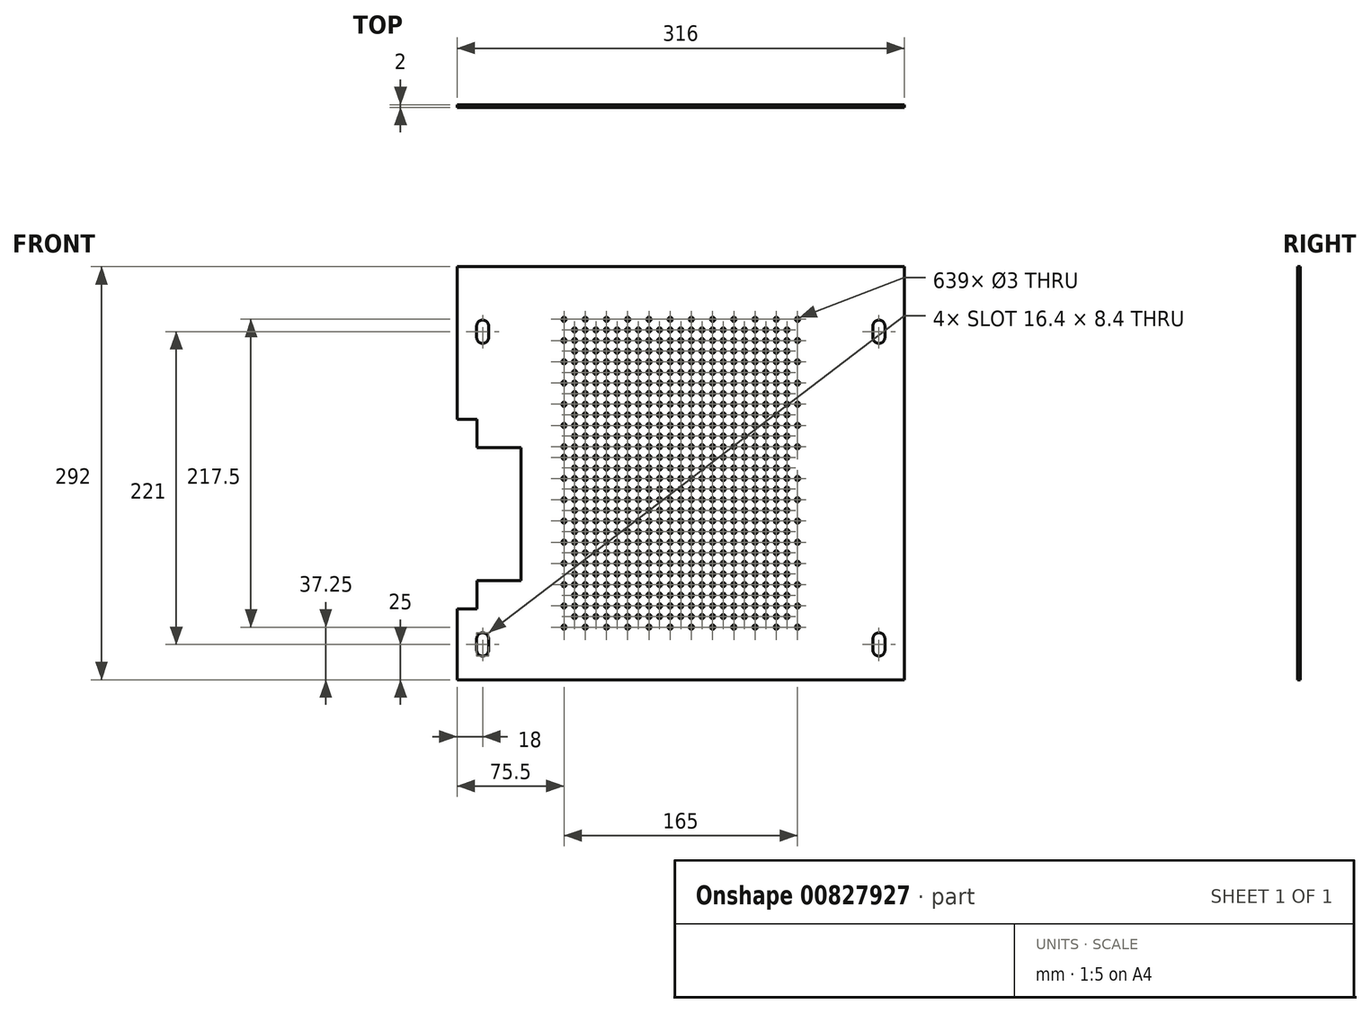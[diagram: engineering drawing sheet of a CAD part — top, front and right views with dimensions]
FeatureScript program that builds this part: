
annotation { "Feature Type Name" : "Feature", "Feature Type Description" : "" }
export const myFeature = defineFeature(function(context is Context, id is Id, definition is map)
    precondition{}
    {
        {
            var Q0;
            Q0=qCreatedBy(makeId("Front.planeOp"),FACE);
            var sketch = newSketch(context, id + "F0", { "sketchPlane" : qUnion([Q0])});
            skLineSegment(sketch, "E0.bottom", {"start": v(158, 146) * mm, "end": v(-158, 146) * mm});
            skLineSegment(sketch, "E0.top", {"start": v(158, -146) * mm, "end": v(-158, -146) * mm});
            skLineSegment(sketch, "E0.left", {"start": v(158, 146) * mm, "end": v(158, -146) * mm});
            skLineSegment(sketch, "E0.right", {"start": v(-158, 146) * mm, "end": v(-158, 38) * mm});
            skPoint(sketch, "E0.middle", {"position": v(0, 0) * mm});
            skLineSegment(sketch, "E1", {"start": v(-113, 18) * mm, "end": v(-113, -76) * mm});
            skLineSegment(sketch, "E2.trimOffspring", {"start": v(-158, -96) * mm, "end": v(-158, -146) * mm});
            skLineSegment(sketch, "E3", {"start": v(-158, 38) * mm, "end": v(-144, 38) * mm});
            skLineSegment(sketch, "E4", {"start": v(-144, 38) * mm, "end": v(-144, 18) * mm});
            skLineSegment(sketch, "E5", {"start": v(-144, 18) * mm, "end": v(-113, 18) * mm});
            skLineSegment(sketch, "E6", {"start": v(-113, -76) * mm, "end": v(-144, -76) * mm});
            skLineSegment(sketch, "E7", {"start": v(-144, -76) * mm, "end": v(-144, -96) * mm});
            skLineSegment(sketch, "E8", {"start": v(-144, -96) * mm, "end": v(-158, -96) * mm});
            skSolve(sketch);
        }
        {
            var Q0;
            Q0 = qSketchRegion(id + "F0", true);
            extrude(context, id + "F1", {"entities" : qUnion([Q0]), "depth" : 2 * mm, "offsetDistance" : 25 * mm});
        }
        {
            var Q0;
            Q0=makeQuery(id+"F1.opExtrude","CAP_FACE",FACE,{"disambiguationData":[OSD([sQuery(id+"F0.wireOp",EDGE,"E0.bottom"),sQuery(id+"F0.wireOp",EDGE,"E0.top"),sQuery(id+"F0.wireOp",EDGE,"E0.left"),sQuery(id+"F0.wireOp",EDGE,"E0.right"),sQuery(id+"F0.wireOp",EDGE,"E1"),sQuery(id+"F0.wireOp",EDGE,"E2.trimOffspring"),sQuery(id+"F0.wireOp",EDGE,"E3"),sQuery(id+"F0.wireOp",EDGE,"E4"),sQuery(id+"F0.wireOp",EDGE,"E5"),sQuery(id+"F0.wireOp",EDGE,"E6"),sQuery(id+"F0.wireOp",EDGE,"E7"),sQuery(id+"F0.wireOp",EDGE,"E8")])],"isStart":false});
            var sketch = newSketch(context, id + "F2", { "sketchPlane" : qUnion([Q0])});
            skLineSegment(sketch, "E9", {"start": v(-140, 100) * mm, "end": v(-140, 104) * mm});
            skLineSegment(sketch, "E10", {"start": v(-140, 100) * mm, "end": v(-140, 96) * mm});
            skArc(sketch, "E11.0.endCap", {"start": v(-144.2, 104) * mm, "mid": v(-140, 108.2) * mm, "end": v(-135.8, 104) * mm});
            skLineSegment(sketch, "E11.0.left", {"start": v(-144.2, 100) * mm, "end": v(-144.2, 104) * mm});
            skLineSegment(sketch, "E11.0.right", {"start": v(-135.8, 100) * mm, "end": v(-135.8, 104) * mm});
            skArc(sketch, "E11.1.endCap", {"start": v(-135.8, 96) * mm, "mid": v(-140, 91.8) * mm, "end": v(-144.2, 96) * mm});
            skLineSegment(sketch, "E11.1.left", {"start": v(-135.8, 100) * mm, "end": v(-135.8, 96) * mm});
            skLineSegment(sketch, "E11.1.right", {"start": v(-144.2, 100) * mm, "end": v(-144.2, 96) * mm});
            skLineSegment(sketch, "E12.MirrorCS", {"start": v(144.2, 100) * mm, "end": v(144.2, 104) * mm});
            skArc(sketch, "E13.MirrorCS", {"start": v(144.2, 104) * mm, "mid": v(140, 108.2) * mm, "end": v(135.8, 104) * mm});
            skLineSegment(sketch, "E14.MirrorCS", {"start": v(135.8, 100) * mm, "end": v(135.8, 104) * mm});
            skLineSegment(sketch, "E15.MirrorCS", {"start": v(135.8, 100) * mm, "end": v(135.8, 96) * mm});
            skArc(sketch, "E16.MirrorCS", {"start": v(135.8, 96) * mm, "mid": v(140, 91.8) * mm, "end": v(144.2, 96) * mm});
            skLineSegment(sketch, "E17.MirrorCS", {"start": v(144.2, 100) * mm, "end": v(144.2, 96) * mm});
            skLineSegment(sketch, "E18", {"start": v(-140, -125) * mm, "end": v(-140, -117) * mm});
            skArc(sketch, "E19.0.startCap", {"start": v(-135.8, -125) * mm, "mid": v(-140, -129.2) * mm, "end": v(-144.2, -125) * mm});
            skArc(sketch, "E19.0.endCap", {"start": v(-144.2, -117) * mm, "mid": v(-140, -112.8) * mm, "end": v(-135.8, -117) * mm});
            skLineSegment(sketch, "E19.0.left", {"start": v(-144.2, -125) * mm, "end": v(-144.2, -117) * mm});
            skLineSegment(sketch, "E19.0.right", {"start": v(-135.8, -125) * mm, "end": v(-135.8, -117) * mm});
            skArc(sketch, "E20.MirrorCS", {"start": v(135.8, -125) * mm, "mid": v(140, -129.2) * mm, "end": v(144.2, -125) * mm});
            skLineSegment(sketch, "E21.MirrorCS", {"start": v(135.8, -125) * mm, "end": v(135.8, -117) * mm});
            skLineSegment(sketch, "E22.MirrorCS", {"start": v(144.2, -125) * mm, "end": v(144.2, -117) * mm});
            skArc(sketch, "E23.MirrorCS", {"start": v(144.2, -117) * mm, "mid": v(140, -112.8) * mm, "end": v(135.8, -117) * mm});
            skSolve(sketch);
        }
        {
            var Q0;
            Q0 = qSketchRegion(id + "F2", true);
            extrude(context, id + "F3", {"entities" : qUnion([Q0]), "operationType" : NewBodyOperationType.REMOVE, "endBound" : BoundingType.THROUGH_ALL, "oppositeDirection" : true, "depth" : 25 * mm, "offsetDistance" : 25 * mm});
        }
        {
            var Q0;
            Q0=makeQuery(id+"F1.opExtrude","CAP_FACE",FACE,{"disambiguationData":[OSD([sQuery(id+"F0.wireOp",EDGE,"E0.bottom"),sQuery(id+"F0.wireOp",EDGE,"E0.top"),sQuery(id+"F0.wireOp",EDGE,"E0.left"),sQuery(id+"F0.wireOp",EDGE,"E0.right"),sQuery(id+"F0.wireOp",EDGE,"E1"),sQuery(id+"F0.wireOp",EDGE,"E2.trimOffspring"),sQuery(id+"F0.wireOp",EDGE,"E3"),sQuery(id+"F0.wireOp",EDGE,"E4"),sQuery(id+"F0.wireOp",EDGE,"E5"),sQuery(id+"F0.wireOp",EDGE,"E6"),sQuery(id+"F0.wireOp",EDGE,"E7"),sQuery(id+"F0.wireOp",EDGE,"E8")])],"isStart":false});
            var sketch = newSketch(context, id + "F4", { "sketchPlane" : qUnion([Q0])});
            skLineSegment(sketch, "E24", {"start": v(0, 0) * mm, "end": v(0, 20.25) * mm});
            skCircle(sketch, "E25", {"center": v(0, 3.75) * mm, "radius": 1.5 * mm});
            skCircle(sketch, "E26.0.1.0", {"center": v(0, 11.25) * mm, "radius": 1.5 * mm});
            skCircle(sketch, "E26.0.2.0", {"center": v(0, 18.75) * mm, "radius": 1.5 * mm});
            skCircle(sketch, "E26.0.3.0", {"center": v(0, 26.25) * mm, "radius": 1.5 * mm});
            skCircle(sketch, "E26.0.4.0", {"center": v(0, 33.75) * mm, "radius": 1.5 * mm});
            skCircle(sketch, "E26.0.5.0", {"center": v(0, 41.25) * mm, "radius": 1.5 * mm});
            skCircle(sketch, "E26.0.6.0", {"center": v(0, 48.75) * mm, "radius": 1.5 * mm});
            skCircle(sketch, "E26.0.7.0", {"center": v(0, 56.25) * mm, "radius": 1.5 * mm});
            skCircle(sketch, "E26.0.8.0", {"center": v(0, 63.75) * mm, "radius": 1.5 * mm});
            skCircle(sketch, "E26.0.9.0", {"center": v(0, 71.25) * mm, "radius": 1.5 * mm});
            skCircle(sketch, "E26.0.10.0", {"center": v(0, 78.75) * mm, "radius": 1.5 * mm});
            skCircle(sketch, "E26.0.11.0", {"center": v(0, 86.25) * mm, "radius": 1.5 * mm});
            skCircle(sketch, "E26.0.12.0", {"center": v(0, 93.75) * mm, "radius": 1.5 * mm});
            skCircle(sketch, "E26.0.13.0", {"center": v(0, 101.25) * mm, "radius": 1.5 * mm});
            skLineSegment(sketch, "E26.direction1", {"start": v(0, 3.75) * mm, "end": v(25, 3.75) * mm, "construction": true});
            skLineSegment(sketch, "E26.direction2", {"start": v(0, 3.75) * mm, "end": v(0, 11.25) * mm, "construction": true});
            skLineSegment(sketch, "E27.1.0.0", {"start": v(7.5, 3.75) * mm, "end": v(7.5, 11.25) * mm, "construction": true});
            skCircle(sketch, "E27.1.0.1", {"center": v(7.5, 86.25) * mm, "radius": 1.5 * mm});
            skCircle(sketch, "E27.1.0.2", {"center": v(7.5, 26.25) * mm, "radius": 1.5 * mm});
            skCircle(sketch, "E27.1.0.3", {"center": v(7.5, 48.75) * mm, "radius": 1.5 * mm});
            skCircle(sketch, "E27.1.0.4", {"center": v(7.5, 101.25) * mm, "radius": 1.5 * mm});
            skCircle(sketch, "E27.1.0.5", {"center": v(7.5, 108.75) * mm, "radius": 1.5 * mm});
            skCircle(sketch, "E27.1.0.6", {"center": v(7.5, 93.75) * mm, "radius": 1.5 * mm});
            skCircle(sketch, "E27.1.0.7", {"center": v(7.5, 18.75) * mm, "radius": 1.5 * mm});
            skCircle(sketch, "E27.1.0.8", {"center": v(7.5, 63.75) * mm, "radius": 1.5 * mm});
            skCircle(sketch, "E27.1.0.9", {"center": v(7.5, 71.25) * mm, "radius": 1.5 * mm});
            skCircle(sketch, "E27.1.0.10", {"center": v(7.5, 56.25) * mm, "radius": 1.5 * mm});
            skCircle(sketch, "E27.1.0.11", {"center": v(7.5, 41.25) * mm, "radius": 1.5 * mm});
            skCircle(sketch, "E27.1.0.12", {"center": v(7.5, 33.75) * mm, "radius": 1.5 * mm});
            skCircle(sketch, "E27.1.0.13", {"center": v(7.5, 78.75) * mm, "radius": 1.5 * mm});
            skCircle(sketch, "E27.1.0.14", {"center": v(7.5, 11.25) * mm, "radius": 1.5 * mm});
            skCircle(sketch, "E27.1.0.15", {"center": v(7.5, 3.75) * mm, "radius": 1.5 * mm});
            skLineSegment(sketch, "E27.2.0.0", {"start": v(15, 3.75) * mm, "end": v(15, 11.25) * mm, "construction": true});
            skCircle(sketch, "E27.2.0.1", {"center": v(15, 86.25) * mm, "radius": 1.5 * mm});
            skCircle(sketch, "E27.2.0.2", {"center": v(15, 26.25) * mm, "radius": 1.5 * mm});
            skCircle(sketch, "E27.2.0.3", {"center": v(15, 48.75) * mm, "radius": 1.5 * mm});
            skCircle(sketch, "E27.2.0.4", {"center": v(15, 101.25) * mm, "radius": 1.5 * mm});
            skCircle(sketch, "E27.2.0.6", {"center": v(15, 93.75) * mm, "radius": 1.5 * mm});
            skCircle(sketch, "E27.2.0.7", {"center": v(15, 18.75) * mm, "radius": 1.5 * mm});
            skCircle(sketch, "E27.2.0.8", {"center": v(15, 63.75) * mm, "radius": 1.5 * mm});
            skCircle(sketch, "E27.2.0.9", {"center": v(15, 71.25) * mm, "radius": 1.5 * mm});
            skCircle(sketch, "E27.2.0.10", {"center": v(15, 56.25) * mm, "radius": 1.5 * mm});
            skCircle(sketch, "E27.2.0.11", {"center": v(15, 41.25) * mm, "radius": 1.5 * mm});
            skCircle(sketch, "E27.2.0.12", {"center": v(15, 33.75) * mm, "radius": 1.5 * mm});
            skCircle(sketch, "E27.2.0.13", {"center": v(15, 78.75) * mm, "radius": 1.5 * mm});
            skCircle(sketch, "E27.2.0.14", {"center": v(15, 11.25) * mm, "radius": 1.5 * mm});
            skCircle(sketch, "E27.2.0.15", {"center": v(15, 3.75) * mm, "radius": 1.5 * mm});
            skLineSegment(sketch, "E27.3.0.0", {"start": v(22.5, 3.75) * mm, "end": v(22.5, 11.25) * mm, "construction": true});
            skCircle(sketch, "E27.3.0.1", {"center": v(22.5, 86.25) * mm, "radius": 1.5 * mm});
            skCircle(sketch, "E27.3.0.2", {"center": v(22.5, 26.25) * mm, "radius": 1.5 * mm});
            skCircle(sketch, "E27.3.0.3", {"center": v(22.5, 48.75) * mm, "radius": 1.5 * mm});
            skCircle(sketch, "E27.3.0.4", {"center": v(22.5, 101.25) * mm, "radius": 1.5 * mm});
            skCircle(sketch, "E27.3.0.5", {"center": v(22.5, 108.75) * mm, "radius": 1.5 * mm});
            skCircle(sketch, "E27.3.0.6", {"center": v(22.5, 93.75) * mm, "radius": 1.5 * mm});
            skCircle(sketch, "E27.3.0.7", {"center": v(22.5, 18.75) * mm, "radius": 1.5 * mm});
            skCircle(sketch, "E27.3.0.8", {"center": v(22.5, 63.75) * mm, "radius": 1.5 * mm});
            skCircle(sketch, "E27.3.0.9", {"center": v(22.5, 71.25) * mm, "radius": 1.5 * mm});
            skCircle(sketch, "E27.3.0.10", {"center": v(22.5, 56.25) * mm, "radius": 1.5 * mm});
            skCircle(sketch, "E27.3.0.11", {"center": v(22.5, 41.25) * mm, "radius": 1.5 * mm});
            skCircle(sketch, "E27.3.0.12", {"center": v(22.5, 33.75) * mm, "radius": 1.5 * mm});
            skCircle(sketch, "E27.3.0.13", {"center": v(22.5, 78.75) * mm, "radius": 1.5 * mm});
            skCircle(sketch, "E27.3.0.14", {"center": v(22.5, 11.25) * mm, "radius": 1.5 * mm});
            skCircle(sketch, "E27.3.0.15", {"center": v(22.5, 3.75) * mm, "radius": 1.5 * mm});
            skLineSegment(sketch, "E27.4.0.0", {"start": v(30, 3.75) * mm, "end": v(30, 11.25) * mm, "construction": true});
            skCircle(sketch, "E27.4.0.1", {"center": v(30, 86.25) * mm, "radius": 1.5 * mm});
            skCircle(sketch, "E27.4.0.2", {"center": v(30, 26.25) * mm, "radius": 1.5 * mm});
            skCircle(sketch, "E27.4.0.3", {"center": v(30, 48.75) * mm, "radius": 1.5 * mm});
            skCircle(sketch, "E27.4.0.4", {"center": v(30, 101.25) * mm, "radius": 1.5 * mm});
            skCircle(sketch, "E27.4.0.6", {"center": v(30, 93.75) * mm, "radius": 1.5 * mm});
            skCircle(sketch, "E27.4.0.7", {"center": v(30, 18.75) * mm, "radius": 1.5 * mm});
            skCircle(sketch, "E27.4.0.8", {"center": v(30, 63.75) * mm, "radius": 1.5 * mm});
            skCircle(sketch, "E27.4.0.9", {"center": v(30, 71.25) * mm, "radius": 1.5 * mm});
            skCircle(sketch, "E27.4.0.10", {"center": v(30, 56.25) * mm, "radius": 1.5 * mm});
            skCircle(sketch, "E27.4.0.11", {"center": v(30, 41.25) * mm, "radius": 1.5 * mm});
            skCircle(sketch, "E27.4.0.12", {"center": v(30, 33.75) * mm, "radius": 1.5 * mm});
            skCircle(sketch, "E27.4.0.13", {"center": v(30, 78.75) * mm, "radius": 1.5 * mm});
            skCircle(sketch, "E27.4.0.14", {"center": v(30, 11.25) * mm, "radius": 1.5 * mm});
            skCircle(sketch, "E27.4.0.15", {"center": v(30, 3.75) * mm, "radius": 1.5 * mm});
            skLineSegment(sketch, "E27.5.0.0", {"start": v(37.5, 3.75) * mm, "end": v(37.5, 11.25) * mm, "construction": true});
            skCircle(sketch, "E27.5.0.1", {"center": v(37.5, 86.25) * mm, "radius": 1.5 * mm});
            skCircle(sketch, "E27.5.0.2", {"center": v(37.5, 26.25) * mm, "radius": 1.5 * mm});
            skCircle(sketch, "E27.5.0.3", {"center": v(37.5, 48.75) * mm, "radius": 1.5 * mm});
            skCircle(sketch, "E27.5.0.4", {"center": v(37.5, 101.25) * mm, "radius": 1.5 * mm});
            skCircle(sketch, "E27.5.0.5", {"center": v(37.5, 108.75) * mm, "radius": 1.5 * mm});
            skCircle(sketch, "E27.5.0.6", {"center": v(37.5, 93.75) * mm, "radius": 1.5 * mm});
            skCircle(sketch, "E27.5.0.7", {"center": v(37.5, 18.75) * mm, "radius": 1.5 * mm});
            skCircle(sketch, "E27.5.0.8", {"center": v(37.5, 63.75) * mm, "radius": 1.5 * mm});
            skCircle(sketch, "E27.5.0.9", {"center": v(37.5, 71.25) * mm, "radius": 1.5 * mm});
            skCircle(sketch, "E27.5.0.10", {"center": v(37.5, 56.25) * mm, "radius": 1.5 * mm});
            skCircle(sketch, "E27.5.0.11", {"center": v(37.5, 41.25) * mm, "radius": 1.5 * mm});
            skCircle(sketch, "E27.5.0.12", {"center": v(37.5, 33.75) * mm, "radius": 1.5 * mm});
            skCircle(sketch, "E27.5.0.13", {"center": v(37.5, 78.75) * mm, "radius": 1.5 * mm});
            skCircle(sketch, "E27.5.0.14", {"center": v(37.5, 11.25) * mm, "radius": 1.5 * mm});
            skCircle(sketch, "E27.5.0.15", {"center": v(37.5, 3.75) * mm, "radius": 1.5 * mm});
            skLineSegment(sketch, "E27.6.0.0", {"start": v(45, 3.75) * mm, "end": v(45, 11.25) * mm, "construction": true});
            skCircle(sketch, "E27.6.0.1", {"center": v(45, 86.25) * mm, "radius": 1.5 * mm});
            skCircle(sketch, "E27.6.0.2", {"center": v(45, 26.25) * mm, "radius": 1.5 * mm});
            skCircle(sketch, "E27.6.0.3", {"center": v(45, 48.75) * mm, "radius": 1.5 * mm});
            skCircle(sketch, "E27.6.0.4", {"center": v(45, 101.25) * mm, "radius": 1.5 * mm});
            skCircle(sketch, "E27.6.0.6", {"center": v(45, 93.75) * mm, "radius": 1.5 * mm});
            skCircle(sketch, "E27.6.0.7", {"center": v(45, 18.75) * mm, "radius": 1.5 * mm});
            skCircle(sketch, "E27.6.0.8", {"center": v(45, 63.75) * mm, "radius": 1.5 * mm});
            skCircle(sketch, "E27.6.0.9", {"center": v(45, 71.25) * mm, "radius": 1.5 * mm});
            skCircle(sketch, "E27.6.0.10", {"center": v(45, 56.25) * mm, "radius": 1.5 * mm});
            skCircle(sketch, "E27.6.0.11", {"center": v(45, 41.25) * mm, "radius": 1.5 * mm});
            skCircle(sketch, "E27.6.0.12", {"center": v(45, 33.75) * mm, "radius": 1.5 * mm});
            skCircle(sketch, "E27.6.0.13", {"center": v(45, 78.75) * mm, "radius": 1.5 * mm});
            skCircle(sketch, "E27.6.0.14", {"center": v(45, 11.25) * mm, "radius": 1.5 * mm});
            skCircle(sketch, "E27.6.0.15", {"center": v(45, 3.75) * mm, "radius": 1.5 * mm});
            skLineSegment(sketch, "E27.7.0.0", {"start": v(52.5, 3.75) * mm, "end": v(52.5, 11.25) * mm, "construction": true});
            skCircle(sketch, "E27.7.0.1", {"center": v(52.5, 86.25) * mm, "radius": 1.5 * mm});
            skCircle(sketch, "E27.7.0.2", {"center": v(52.5, 26.25) * mm, "radius": 1.5 * mm});
            skCircle(sketch, "E27.7.0.3", {"center": v(52.5, 48.75) * mm, "radius": 1.5 * mm});
            skCircle(sketch, "E27.7.0.4", {"center": v(52.5, 101.25) * mm, "radius": 1.5 * mm});
            skCircle(sketch, "E27.7.0.5", {"center": v(52.5, 108.75) * mm, "radius": 1.5 * mm});
            skCircle(sketch, "E27.7.0.6", {"center": v(52.5, 93.75) * mm, "radius": 1.5 * mm});
            skCircle(sketch, "E27.7.0.7", {"center": v(52.5, 18.75) * mm, "radius": 1.5 * mm});
            skCircle(sketch, "E27.7.0.8", {"center": v(52.5, 63.75) * mm, "radius": 1.5 * mm});
            skCircle(sketch, "E27.7.0.9", {"center": v(52.5, 71.25) * mm, "radius": 1.5 * mm});
            skCircle(sketch, "E27.7.0.10", {"center": v(52.5, 56.25) * mm, "radius": 1.5 * mm});
            skCircle(sketch, "E27.7.0.11", {"center": v(52.5, 41.25) * mm, "radius": 1.5 * mm});
            skCircle(sketch, "E27.7.0.12", {"center": v(52.5, 33.75) * mm, "radius": 1.5 * mm});
            skCircle(sketch, "E27.7.0.13", {"center": v(52.5, 78.75) * mm, "radius": 1.5 * mm});
            skCircle(sketch, "E27.7.0.14", {"center": v(52.5, 11.25) * mm, "radius": 1.5 * mm});
            skCircle(sketch, "E27.7.0.15", {"center": v(52.5, 3.75) * mm, "radius": 1.5 * mm});
            skLineSegment(sketch, "E27.8.0.0", {"start": v(60, 3.75) * mm, "end": v(60, 11.25) * mm, "construction": true});
            skCircle(sketch, "E27.8.0.1", {"center": v(60, 86.25) * mm, "radius": 1.5 * mm});
            skCircle(sketch, "E27.8.0.2", {"center": v(60, 26.25) * mm, "radius": 1.5 * mm});
            skCircle(sketch, "E27.8.0.3", {"center": v(60, 48.75) * mm, "radius": 1.5 * mm});
            skCircle(sketch, "E27.8.0.4", {"center": v(60, 101.25) * mm, "radius": 1.5 * mm});
            skCircle(sketch, "E27.8.0.6", {"center": v(60, 93.75) * mm, "radius": 1.5 * mm});
            skCircle(sketch, "E27.8.0.7", {"center": v(60, 18.75) * mm, "radius": 1.5 * mm});
            skCircle(sketch, "E27.8.0.8", {"center": v(60, 63.75) * mm, "radius": 1.5 * mm});
            skCircle(sketch, "E27.8.0.9", {"center": v(60, 71.25) * mm, "radius": 1.5 * mm});
            skCircle(sketch, "E27.8.0.10", {"center": v(60, 56.25) * mm, "radius": 1.5 * mm});
            skCircle(sketch, "E27.8.0.11", {"center": v(60, 41.25) * mm, "radius": 1.5 * mm});
            skCircle(sketch, "E27.8.0.12", {"center": v(60, 33.75) * mm, "radius": 1.5 * mm});
            skCircle(sketch, "E27.8.0.13", {"center": v(60, 78.75) * mm, "radius": 1.5 * mm});
            skCircle(sketch, "E27.8.0.14", {"center": v(60, 11.25) * mm, "radius": 1.5 * mm});
            skCircle(sketch, "E27.8.0.15", {"center": v(60, 3.75) * mm, "radius": 1.5 * mm});
            skLineSegment(sketch, "E27.9.0.0", {"start": v(67.5, 3.75) * mm, "end": v(67.5, 11.25) * mm, "construction": true});
            skCircle(sketch, "E27.9.0.1", {"center": v(67.5, 86.25) * mm, "radius": 1.5 * mm});
            skCircle(sketch, "E27.9.0.2", {"center": v(67.5, 26.25) * mm, "radius": 1.5 * mm});
            skCircle(sketch, "E27.9.0.3", {"center": v(67.5, 48.75) * mm, "radius": 1.5 * mm});
            skCircle(sketch, "E27.9.0.4", {"center": v(67.5, 101.25) * mm, "radius": 1.5 * mm});
            skCircle(sketch, "E27.9.0.5", {"center": v(67.5, 108.75) * mm, "radius": 1.5 * mm});
            skCircle(sketch, "E27.9.0.6", {"center": v(67.5, 93.75) * mm, "radius": 1.5 * mm});
            skCircle(sketch, "E27.9.0.7", {"center": v(67.5, 18.75) * mm, "radius": 1.5 * mm});
            skCircle(sketch, "E27.9.0.8", {"center": v(67.5, 63.75) * mm, "radius": 1.5 * mm});
            skCircle(sketch, "E27.9.0.9", {"center": v(67.5, 71.25) * mm, "radius": 1.5 * mm});
            skCircle(sketch, "E27.9.0.10", {"center": v(67.5, 56.25) * mm, "radius": 1.5 * mm});
            skCircle(sketch, "E27.9.0.11", {"center": v(67.5, 41.25) * mm, "radius": 1.5 * mm});
            skCircle(sketch, "E27.9.0.12", {"center": v(67.5, 33.75) * mm, "radius": 1.5 * mm});
            skCircle(sketch, "E27.9.0.13", {"center": v(67.5, 78.75) * mm, "radius": 1.5 * mm});
            skCircle(sketch, "E27.9.0.14", {"center": v(67.5, 11.25) * mm, "radius": 1.5 * mm});
            skCircle(sketch, "E27.9.0.15", {"center": v(67.5, 3.75) * mm, "radius": 1.5 * mm});
            skLineSegment(sketch, "E27.10.0.0", {"start": v(75, 3.75) * mm, "end": v(75, 11.25) * mm, "construction": true});
            skCircle(sketch, "E27.10.0.1", {"center": v(75, 86.25) * mm, "radius": 1.5 * mm});
            skCircle(sketch, "E27.10.0.2", {"center": v(75, 26.25) * mm, "radius": 1.5 * mm});
            skCircle(sketch, "E27.10.0.3", {"center": v(75, 48.75) * mm, "radius": 1.5 * mm});
            skCircle(sketch, "E27.10.0.4", {"center": v(75, 101.25) * mm, "radius": 1.5 * mm});
            skCircle(sketch, "E27.10.0.6", {"center": v(75, 93.75) * mm, "radius": 1.5 * mm});
            skCircle(sketch, "E27.10.0.7", {"center": v(75, 18.75) * mm, "radius": 1.5 * mm});
            skCircle(sketch, "E27.10.0.8", {"center": v(75, 63.75) * mm, "radius": 1.5 * mm});
            skCircle(sketch, "E27.10.0.9", {"center": v(75, 71.25) * mm, "radius": 1.5 * mm});
            skCircle(sketch, "E27.10.0.10", {"center": v(75, 56.25) * mm, "radius": 1.5 * mm});
            skCircle(sketch, "E27.10.0.11", {"center": v(75, 41.25) * mm, "radius": 1.5 * mm});
            skCircle(sketch, "E27.10.0.12", {"center": v(75, 33.75) * mm, "radius": 1.5 * mm});
            skCircle(sketch, "E27.10.0.13", {"center": v(75, 78.75) * mm, "radius": 1.5 * mm});
            skCircle(sketch, "E27.10.0.14", {"center": v(75, 11.25) * mm, "radius": 1.5 * mm});
            skCircle(sketch, "E27.10.0.15", {"center": v(75, 3.75) * mm, "radius": 1.5 * mm});
            skLineSegment(sketch, "E27.11.0.0", {"start": v(82.5, 3.75) * mm, "end": v(82.5, 11.25) * mm, "construction": true});
            skCircle(sketch, "E27.11.0.3", {"center": v(82.5, 48.75) * mm, "radius": 1.5 * mm});
            skCircle(sketch, "E27.11.0.5", {"center": v(82.5, 108.75) * mm, "radius": 1.5 * mm});
            skCircle(sketch, "E27.11.0.6", {"center": v(82.5, 93.75) * mm, "radius": 1.5 * mm});
            skCircle(sketch, "E27.11.0.7", {"center": v(82.5, 18.75) * mm, "radius": 1.5 * mm});
            skCircle(sketch, "E27.11.0.8", {"center": v(82.5, 63.75) * mm, "radius": 1.5 * mm});
            skCircle(sketch, "E27.11.0.12", {"center": v(82.5, 33.75) * mm, "radius": 1.5 * mm});
            skCircle(sketch, "E27.11.0.13", {"center": v(82.5, 78.75) * mm, "radius": 1.5 * mm});
            skLineSegment(sketch, "E27.direction1", {"start": v(0, 3.75) * mm, "end": v(7.5, 3.75) * mm, "construction": true});
            skLineSegment(sketch, "E28.trimOffspring", {"start": v(0, 107.25) * mm, "end": v(0, 110.25) * mm});
            skLineSegment(sketch, "E29.trimOffspring", {"start": v(0, 99.75) * mm, "end": v(0, 102.75) * mm});
            skLineSegment(sketch, "E30.trimOffspring", {"start": v(0, 92.25) * mm, "end": v(0, 95.25) * mm});
            skLineSegment(sketch, "E31.trimOffspring", {"start": v(0, 84.75) * mm, "end": v(0, 87.75) * mm});
            skLineSegment(sketch, "E32.trimOffspring", {"start": v(0, 77.25) * mm, "end": v(0, 80.25) * mm});
            skLineSegment(sketch, "E33.trimOffspring", {"start": v(0, 69.75) * mm, "end": v(0, 72.75) * mm});
            skLineSegment(sketch, "E34.trimOffspring", {"start": v(0, 62.25) * mm, "end": v(0, 65.25) * mm});
            skLineSegment(sketch, "E35.trimOffspring", {"start": v(0, 54.75) * mm, "end": v(0, 57.75) * mm});
            skCircle(sketch, "E36.MirrorC", {"center": v(-7.5, 3.75) * mm, "radius": 1.5 * mm});
            skCircle(sketch, "E37.MirrorC", {"center": v(-15, 3.75) * mm, "radius": 1.5 * mm});
            skCircle(sketch, "E38.MirrorC", {"center": v(-7.5, 11.25) * mm, "radius": 1.5 * mm});
            skCircle(sketch, "E39.MirrorC", {"center": v(-22.5, 3.75) * mm, "radius": 1.5 * mm});
            skCircle(sketch, "E40.MirrorC", {"center": v(-67.5, 3.75) * mm, "radius": 1.5 * mm});
            skCircle(sketch, "E41.MirrorC", {"center": v(-60, 11.25) * mm, "radius": 1.5 * mm});
            skCircle(sketch, "E42.MirrorC", {"center": v(-15, 11.25) * mm, "radius": 1.5 * mm});
            skCircle(sketch, "E43.MirrorC", {"center": v(-75, 11.25) * mm, "radius": 1.5 * mm});
            skCircle(sketch, "E44.MirrorC", {"center": v(-45, 3.75) * mm, "radius": 1.5 * mm});
            skCircle(sketch, "E45.MirrorC", {"center": v(-30, 3.75) * mm, "radius": 1.5 * mm});
            skCircle(sketch, "E46.MirrorC", {"center": v(-82.5, 11.25) * mm, "radius": 1.5 * mm});
            skCircle(sketch, "E47.MirrorC", {"center": v(-75, 3.75) * mm, "radius": 1.5 * mm});
            skCircle(sketch, "E48.MirrorC", {"center": v(-22.5, 11.25) * mm, "radius": 1.5 * mm});
            skCircle(sketch, "E49.MirrorC", {"center": v(-45, 11.25) * mm, "radius": 1.5 * mm});
            skCircle(sketch, "E50.MirrorC", {"center": v(-60, 3.75) * mm, "radius": 1.5 * mm});
            skCircle(sketch, "E51.MirrorC", {"center": v(-37.5, 3.75) * mm, "radius": 1.5 * mm});
            skCircle(sketch, "E52.MirrorC", {"center": v(-67.5, 11.25) * mm, "radius": 1.5 * mm});
            skCircle(sketch, "E53.MirrorC", {"center": v(-30, 11.25) * mm, "radius": 1.5 * mm});
            skCircle(sketch, "E54.MirrorC", {"center": v(-52.5, 3.75) * mm, "radius": 1.5 * mm});
            skCircle(sketch, "E55.MirrorC", {"center": v(-37.5, 11.25) * mm, "radius": 1.5 * mm});
            skCircle(sketch, "E56.MirrorC", {"center": v(-52.5, 11.25) * mm, "radius": 1.5 * mm});
            skCircle(sketch, "E57.MirrorC", {"center": v(-30, 86.25) * mm, "radius": 1.5 * mm});
            skCircle(sketch, "E58.MirrorC", {"center": v(-52.5, 48.75) * mm, "radius": 1.5 * mm});
            skCircle(sketch, "E59.MirrorC", {"center": v(-7.5, 78.75) * mm, "radius": 1.5 * mm});
            skCircle(sketch, "E60.MirrorC", {"center": v(-60, 101.25) * mm, "radius": 1.5 * mm});
            skCircle(sketch, "E61.MirrorC", {"center": v(-45, 26.25) * mm, "radius": 1.5 * mm});
            skCircle(sketch, "E62.MirrorC", {"center": v(-37.5, 86.25) * mm, "radius": 1.5 * mm});
            skCircle(sketch, "E63.MirrorC", {"center": v(-82.5, 18.75) * mm, "radius": 1.5 * mm});
            skCircle(sketch, "E64.MirrorC", {"center": v(-75, 93.75) * mm, "radius": 1.5 * mm});
            skCircle(sketch, "E65.MirrorC", {"center": v(-67.5, 108.75) * mm, "radius": 1.5 * mm});
            skCircle(sketch, "E66.MirrorC", {"center": v(-52.5, 101.25) * mm, "radius": 1.5 * mm});
            skCircle(sketch, "E67.MirrorC", {"center": v(-45, 48.75) * mm, "radius": 1.5 * mm});
            skCircle(sketch, "E68.MirrorC", {"center": v(-37.5, 26.25) * mm, "radius": 1.5 * mm});
            skCircle(sketch, "E69.MirrorC", {"center": v(-82.5, 63.75) * mm, "radius": 1.5 * mm});
            skCircle(sketch, "E70.MirrorC", {"center": v(-75, 18.75) * mm, "radius": 1.5 * mm});
            skCircle(sketch, "E71.MirrorC", {"center": v(-67.5, 93.75) * mm, "radius": 1.5 * mm});
            skCircle(sketch, "E72.MirrorC", {"center": v(-30, 26.25) * mm, "radius": 1.5 * mm});
            skCircle(sketch, "E73.MirrorC", {"center": v(-22.5, 86.25) * mm, "radius": 1.5 * mm});
            skCircle(sketch, "E74.MirrorC", {"center": v(-60, 93.75) * mm, "radius": 1.5 * mm});
            skCircle(sketch, "E75.MirrorC", {"center": v(-52.5, 108.75) * mm, "radius": 1.5 * mm});
            skCircle(sketch, "E76.MirrorC", {"center": v(-45, 101.25) * mm, "radius": 1.5 * mm});
            skCircle(sketch, "E77.MirrorC", {"center": v(-37.5, 48.75) * mm, "radius": 1.5 * mm});
            skCircle(sketch, "E78.MirrorC", {"center": v(-75, 63.75) * mm, "radius": 1.5 * mm});
            skCircle(sketch, "E79.MirrorC", {"center": v(-67.5, 18.75) * mm, "radius": 1.5 * mm});
            skCircle(sketch, "E80.MirrorC", {"center": v(-30, 48.75) * mm, "radius": 1.5 * mm});
            skCircle(sketch, "E81.MirrorC", {"center": v(-22.5, 26.25) * mm, "radius": 1.5 * mm});
            skCircle(sketch, "E82.MirrorC", {"center": v(-15, 86.25) * mm, "radius": 1.5 * mm});
            skCircle(sketch, "E83.MirrorC", {"center": v(-60, 18.75) * mm, "radius": 1.5 * mm});
            skCircle(sketch, "E84.MirrorC", {"center": v(-52.5, 93.75) * mm, "radius": 1.5 * mm});
            skCircle(sketch, "E85.MirrorC", {"center": v(-37.5, 101.25) * mm, "radius": 1.5 * mm});
            skCircle(sketch, "E86.MirrorC", {"center": v(-75, 71.25) * mm, "radius": 1.5 * mm});
            skCircle(sketch, "E87.MirrorC", {"center": v(-67.5, 63.75) * mm, "radius": 1.5 * mm});
            skCircle(sketch, "E88.MirrorC", {"center": v(-30, 101.25) * mm, "radius": 1.5 * mm});
            skCircle(sketch, "E89.MirrorC", {"center": v(-22.5, 48.75) * mm, "radius": 1.5 * mm});
            skCircle(sketch, "E90.MirrorC", {"center": v(-15, 26.25) * mm, "radius": 1.5 * mm});
            skCircle(sketch, "E91.MirrorC", {"center": v(-7.5, 86.25) * mm, "radius": 1.5 * mm});
            skCircle(sketch, "E92.MirrorC", {"center": v(-60, 63.75) * mm, "radius": 1.5 * mm});
            skCircle(sketch, "E93.MirrorC", {"center": v(-52.5, 18.75) * mm, "radius": 1.5 * mm});
            skCircle(sketch, "E94.MirrorC", {"center": v(-45, 93.75) * mm, "radius": 1.5 * mm});
            skCircle(sketch, "E95.MirrorC", {"center": v(-37.5, 108.75) * mm, "radius": 1.5 * mm});
            skCircle(sketch, "E96.MirrorC", {"center": v(-75, 56.25) * mm, "radius": 1.5 * mm});
            skCircle(sketch, "E97.MirrorC", {"center": v(-67.5, 71.25) * mm, "radius": 1.5 * mm});
            skCircle(sketch, "E98.MirrorC", {"center": v(-22.5, 101.25) * mm, "radius": 1.5 * mm});
            skCircle(sketch, "E99.MirrorC", {"center": v(-15, 48.75) * mm, "radius": 1.5 * mm});
            skCircle(sketch, "E100.MirrorC", {"center": v(-7.5, 26.25) * mm, "radius": 1.5 * mm});
            skCircle(sketch, "E101.MirrorC", {"center": v(-60, 71.25) * mm, "radius": 1.5 * mm});
            skCircle(sketch, "E102.MirrorC", {"center": v(-52.5, 63.75) * mm, "radius": 1.5 * mm});
            skCircle(sketch, "E103.MirrorC", {"center": v(-45, 18.75) * mm, "radius": 1.5 * mm});
            skCircle(sketch, "E104.MirrorC", {"center": v(-37.5, 93.75) * mm, "radius": 1.5 * mm});
            skCircle(sketch, "E105.MirrorC", {"center": v(-82.5, 33.75) * mm, "radius": 1.5 * mm});
            skCircle(sketch, "E106.MirrorC", {"center": v(-75, 41.25) * mm, "radius": 1.5 * mm});
            skCircle(sketch, "E107.MirrorC", {"center": v(-67.5, 56.25) * mm, "radius": 1.5 * mm});
            skCircle(sketch, "E108.MirrorC", {"center": v(-7.5, 18.75) * mm, "radius": 1.5 * mm});
            skCircle(sketch, "E109.MirrorC", {"center": v(-37.5, 41.25) * mm, "radius": 1.5 * mm});
            skCircle(sketch, "E110.MirrorC", {"center": v(-30, 56.25) * mm, "radius": 1.5 * mm});
            skCircle(sketch, "E111.MirrorC", {"center": v(-22.5, 71.25) * mm, "radius": 1.5 * mm});
            skCircle(sketch, "E112.MirrorC", {"center": v(-15, 63.75) * mm, "radius": 1.5 * mm});
            skCircle(sketch, "E113.MirrorC", {"center": v(-52.5, 78.75) * mm, "radius": 1.5 * mm});
            skCircle(sketch, "E114.MirrorC", {"center": v(-45, 33.75) * mm, "radius": 1.5 * mm});
            skCircle(sketch, "E115.MirrorC", {"center": v(-30, 93.75) * mm, "radius": 1.5 * mm});
            skCircle(sketch, "E116.MirrorC", {"center": v(-22.5, 108.75) * mm, "radius": 1.5 * mm});
            skCircle(sketch, "E117.MirrorC", {"center": v(-15, 101.25) * mm, "radius": 1.5 * mm});
            skCircle(sketch, "E118.MirrorC", {"center": v(-7.5, 48.75) * mm, "radius": 1.5 * mm});
            skCircle(sketch, "E119.MirrorC", {"center": v(-60, 56.25) * mm, "radius": 1.5 * mm});
            skCircle(sketch, "E120.MirrorC", {"center": v(-52.5, 71.25) * mm, "radius": 1.5 * mm});
            skCircle(sketch, "E121.MirrorC", {"center": v(-45, 63.75) * mm, "radius": 1.5 * mm});
            skCircle(sketch, "E122.MirrorC", {"center": v(-37.5, 18.75) * mm, "radius": 1.5 * mm});
            skCircle(sketch, "E123.MirrorC", {"center": v(-82.5, 78.75) * mm, "radius": 1.5 * mm});
            skCircle(sketch, "E124.MirrorC", {"center": v(-75, 33.75) * mm, "radius": 1.5 * mm});
            skCircle(sketch, "E125.MirrorC", {"center": v(-67.5, 41.25) * mm, "radius": 1.5 * mm});
            skCircle(sketch, "E126.MirrorC", {"center": v(-7.5, 108.75) * mm, "radius": 1.5 * mm});
            skCircle(sketch, "E127.MirrorC", {"center": v(-37.5, 71.25) * mm, "radius": 1.5 * mm});
            skCircle(sketch, "E128.MirrorC", {"center": v(-30, 63.75) * mm, "radius": 1.5 * mm});
            skCircle(sketch, "E129.MirrorC", {"center": v(-22.5, 18.75) * mm, "radius": 1.5 * mm});
            skCircle(sketch, "E130.MirrorC", {"center": v(-15, 93.75) * mm, "radius": 1.5 * mm});
            skCircle(sketch, "E131.MirrorC", {"center": v(-67.5, 78.75) * mm, "radius": 1.5 * mm});
            skCircle(sketch, "E132.MirrorC", {"center": v(-60, 33.75) * mm, "radius": 1.5 * mm});
            skCircle(sketch, "E133.MirrorC", {"center": v(-52.5, 41.25) * mm, "radius": 1.5 * mm});
            skCircle(sketch, "E134.MirrorC", {"center": v(-45, 56.25) * mm, "radius": 1.5 * mm});
            skCircle(sketch, "E135.MirrorC", {"center": v(-60, 86.25) * mm, "radius": 1.5 * mm});
            skCircle(sketch, "E136.MirrorC", {"center": v(-82.5, 108.75) * mm, "radius": 1.5 * mm});
            skCircle(sketch, "E137.MirrorC", {"center": v(-7.5, 56.25) * mm, "radius": 1.5 * mm});
            skCircle(sketch, "E138.MirrorC", {"center": v(-75, 78.75) * mm, "radius": 1.5 * mm});
            skCircle(sketch, "E139.MirrorC", {"center": v(-37.5, 63.75) * mm, "radius": 1.5 * mm});
            skCircle(sketch, "E140.MirrorC", {"center": v(-52.5, 56.25) * mm, "radius": 1.5 * mm});
            skCircle(sketch, "E141.MirrorC", {"center": v(-7.5, 101.25) * mm, "radius": 1.5 * mm});
            skCircle(sketch, "E142.MirrorC", {"center": v(-15, 78.75) * mm, "radius": 1.5 * mm});
            skCircle(sketch, "E143.MirrorC", {"center": v(-60, 41.25) * mm, "radius": 1.5 * mm});
            skCircle(sketch, "E144.MirrorC", {"center": v(-22.5, 56.25) * mm, "radius": 1.5 * mm});
            skCircle(sketch, "E145.MirrorC", {"center": v(-52.5, 33.75) * mm, "radius": 1.5 * mm});
            skCircle(sketch, "E146.MirrorC", {"center": v(-30, 41.25) * mm, "radius": 1.5 * mm});
            skCircle(sketch, "E147.MirrorC", {"center": v(-67.5, 48.75) * mm, "radius": 1.5 * mm});
            skCircle(sketch, "E148.MirrorC", {"center": v(-30, 18.75) * mm, "radius": 1.5 * mm});
            skCircle(sketch, "E149.MirrorC", {"center": v(-45, 78.75) * mm, "radius": 1.5 * mm});
            skCircle(sketch, "E150.MirrorC", {"center": v(-45, 41.25) * mm, "radius": 1.5 * mm});
            skCircle(sketch, "E151.MirrorC", {"center": v(-67.5, 26.25) * mm, "radius": 1.5 * mm});
            skCircle(sketch, "E152.MirrorC", {"center": v(-82.5, 48.75) * mm, "radius": 1.5 * mm});
            skCircle(sketch, "E153.MirrorC", {"center": v(-22.5, 63.75) * mm, "radius": 1.5 * mm});
            skCircle(sketch, "E154.MirrorC", {"center": v(-67.5, 86.25) * mm, "radius": 1.5 * mm});
            skCircle(sketch, "E155.MirrorC", {"center": v(-15, 18.75) * mm, "radius": 1.5 * mm});
            skCircle(sketch, "E156.MirrorC", {"center": v(-22.5, 93.75) * mm, "radius": 1.5 * mm});
            skCircle(sketch, "E157.MirrorC", {"center": v(-37.5, 78.75) * mm, "radius": 1.5 * mm});
            skCircle(sketch, "E158.MirrorC", {"center": v(-22.5, 78.75) * mm, "radius": 1.5 * mm});
            skCircle(sketch, "E159.MirrorC", {"center": v(-30, 33.75) * mm, "radius": 1.5 * mm});
            skCircle(sketch, "E160.MirrorC", {"center": v(-15, 71.25) * mm, "radius": 1.5 * mm});
            skCircle(sketch, "E161.MirrorC", {"center": v(-75, 86.25) * mm, "radius": 1.5 * mm});
            skCircle(sketch, "E162.MirrorC", {"center": v(-75, 26.25) * mm, "radius": 1.5 * mm});
            skCircle(sketch, "E163.MirrorC", {"center": v(-7.5, 33.75) * mm, "radius": 1.5 * mm});
            skCircle(sketch, "E164.MirrorC", {"center": v(-45, 86.25) * mm, "radius": 1.5 * mm});
            skCircle(sketch, "E165.MirrorC", {"center": v(-15, 56.25) * mm, "radius": 1.5 * mm});
            skCircle(sketch, "E166.MirrorC", {"center": v(-60, 48.75) * mm, "radius": 1.5 * mm});
            skCircle(sketch, "E167.MirrorC", {"center": v(-52.5, 26.25) * mm, "radius": 1.5 * mm});
            skCircle(sketch, "E168.MirrorC", {"center": v(-60, 78.75) * mm, "radius": 1.5 * mm});
            skCircle(sketch, "E169.MirrorC", {"center": v(-15, 33.75) * mm, "radius": 1.5 * mm});
            skCircle(sketch, "E170.MirrorC", {"center": v(-67.5, 33.75) * mm, "radius": 1.5 * mm});
            skCircle(sketch, "E171.MirrorC", {"center": v(-15, 41.25) * mm, "radius": 1.5 * mm});
            skCircle(sketch, "E172.MirrorC", {"center": v(-30, 78.75) * mm, "radius": 1.5 * mm});
            skCircle(sketch, "E173.MirrorC", {"center": v(-67.5, 101.25) * mm, "radius": 1.5 * mm});
            skCircle(sketch, "E174.MirrorC", {"center": v(-7.5, 71.25) * mm, "radius": 1.5 * mm});
            skCircle(sketch, "E175.MirrorC", {"center": v(-37.5, 33.75) * mm, "radius": 1.5 * mm});
            skCircle(sketch, "E176.MirrorC", {"center": v(-7.5, 41.25) * mm, "radius": 1.5 * mm});
            skCircle(sketch, "E177.MirrorC", {"center": v(-45, 71.25) * mm, "radius": 1.5 * mm});
            skCircle(sketch, "E178.MirrorC", {"center": v(-22.5, 41.25) * mm, "radius": 1.5 * mm});
            skCircle(sketch, "E179.MirrorC", {"center": v(-22.5, 33.75) * mm, "radius": 1.5 * mm});
            skCircle(sketch, "E180.MirrorC", {"center": v(-37.5, 56.25) * mm, "radius": 1.5 * mm});
            skCircle(sketch, "E181.MirrorC", {"center": v(-30, 71.25) * mm, "radius": 1.5 * mm});
            skCircle(sketch, "E182.MirrorC", {"center": v(-52.5, 86.25) * mm, "radius": 1.5 * mm});
            skCircle(sketch, "E183.MirrorC", {"center": v(-7.5, 93.75) * mm, "radius": 1.5 * mm});
            skCircle(sketch, "E184.MirrorC", {"center": v(-7.5, 63.75) * mm, "radius": 1.5 * mm});
            skCircle(sketch, "E185.MirrorC", {"center": v(-75, 101.25) * mm, "radius": 1.5 * mm});
            skCircle(sketch, "E186.MirrorC", {"center": v(-75, 48.75) * mm, "radius": 1.5 * mm});
            skCircle(sketch, "E187.MirrorC", {"center": v(-60, 26.25) * mm, "radius": 1.5 * mm});
            skCircle(sketch, "E188.MirrorC", {"center": v(-82.5, 93.75) * mm, "radius": 1.5 * mm});
            skLineSegment(sketch, "E189.MirrorCS", {"start": v(-67.5, 3.75) * mm, "end": v(-67.5, 11.25) * mm, "construction": true});
            skLineSegment(sketch, "E190.MirrorCS", {"start": v(-52.5, 3.75) * mm, "end": v(-52.5, 11.25) * mm, "construction": true});
            skLineSegment(sketch, "E191.MirrorCS", {"start": v(-30, 3.75) * mm, "end": v(-30, 11.25) * mm, "construction": true});
            skLineSegment(sketch, "E192.MirrorCS", {"start": v(-75, 3.75) * mm, "end": v(-75, 11.25) * mm, "construction": true});
            skLineSegment(sketch, "E193.MirrorCS", {"start": v(-45, 3.75) * mm, "end": v(-45, 11.25) * mm, "construction": true});
            skLineSegment(sketch, "E194.MirrorCS", {"start": v(-60, 3.75) * mm, "end": v(-60, 11.25) * mm, "construction": true});
            skLineSegment(sketch, "E195.MirrorCS", {"start": v(-37.5, 3.75) * mm, "end": v(-37.5, 11.25) * mm, "construction": true});
            skLineSegment(sketch, "E196.MirrorCS", {"start": v(-22.5, 3.75) * mm, "end": v(-22.5, 11.25) * mm, "construction": true});
            skLineSegment(sketch, "E197.MirrorCS", {"start": v(-15, 3.75) * mm, "end": v(-15, 11.25) * mm, "construction": true});
            skLineSegment(sketch, "E198.MirrorCS", {"start": v(-82.5, 3.75) * mm, "end": v(-82.5, 11.25) * mm, "construction": true});
            skLineSegment(sketch, "E199.MirrorCS", {"start": v(-7.5, 3.75) * mm, "end": v(-7.5, 11.25) * mm, "construction": true});
            skLineSegment(sketch, "E200.trimOffspring", {"start": v(0, 39.75) * mm, "end": v(0, 50.25) * mm});
            skLineSegment(sketch, "E201.trimOffspring", {"start": v(0, 32.25) * mm, "end": v(0, 33.75) * mm});
            skLineSegment(sketch, "E202.trimOffspring", {"start": v(0, 24.75) * mm, "end": v(0, 27.75) * mm});
            skLineSegment(sketch, "E203.MirrorCS", {"start": v(0, -77.25) * mm, "end": v(0, -80.25) * mm});
            skLineSegment(sketch, "E204.MirrorCS", {"start": v(0, -24.75) * mm, "end": v(0, -27.75) * mm});
            skLineSegment(sketch, "E205.MirrorCS", {"start": v(0, -54.75) * mm, "end": v(0, -57.75) * mm});
            skCircle(sketch, "E206.MirrorC", {"center": v(0, -3.75) * mm, "radius": 1.5 * mm});
            skLineSegment(sketch, "E207.MirrorCS", {"start": v(0, -99.75) * mm, "end": v(0, -102.75) * mm});
            skCircle(sketch, "E208.MirrorC", {"center": v(0, -56.25) * mm, "radius": 1.5 * mm});
            skCircle(sketch, "E209.MirrorC", {"center": v(0, -101.25) * mm, "radius": 1.5 * mm});
            skCircle(sketch, "E210.MirrorC", {"center": v(0, -26.25) * mm, "radius": 1.5 * mm});
            skLineSegment(sketch, "E211.MirrorCS", {"start": v(0, -84.75) * mm, "end": v(0, -87.75) * mm});
            skCircle(sketch, "E212.MirrorC", {"center": v(0, -78.75) * mm, "radius": 1.5 * mm});
            skCircle(sketch, "E213.MirrorC", {"center": v(7.5, -3.75) * mm, "radius": 1.5 * mm});
            skCircle(sketch, "E214.MirrorC", {"center": v(0, -33.75) * mm, "radius": 1.5 * mm});
            skLineSegment(sketch, "E215.MirrorCS", {"start": v(0, -32.25) * mm, "end": v(0, -33.75) * mm});
            skLineSegment(sketch, "E216.MirrorCS", {"start": v(0, -3.75) * mm, "end": v(7.5, -3.75) * mm, "construction": true});
            skLineSegment(sketch, "E217.MirrorCS", {"start": v(0, -69.75) * mm, "end": v(0, -72.75) * mm});
            skCircle(sketch, "E218.MirrorC", {"center": v(52.5, -11.25) * mm, "radius": 1.5 * mm});
            skCircle(sketch, "E219.MirrorC", {"center": v(45, -11.25) * mm, "radius": 1.5 * mm});
            skCircle(sketch, "E220.MirrorC", {"center": v(75, -3.75) * mm, "radius": 1.5 * mm});
            skLineSegment(sketch, "E221.MirrorCS", {"start": v(22.5, -3.75) * mm, "end": v(22.5, -11.25) * mm, "construction": true});
            skLineSegment(sketch, "E222.MirrorCS", {"start": v(0, -107.25) * mm, "end": v(0, -110.25) * mm});
            skLineSegment(sketch, "E223.MirrorCS", {"start": v(-60, -3.75) * mm, "end": v(-60, -11.25) * mm, "construction": true});
            skCircle(sketch, "E224.MirrorC", {"center": v(-67.5, -3.75) * mm, "radius": 1.5 * mm});
            skLineSegment(sketch, "E225.MirrorCS", {"start": v(-30, -3.75) * mm, "end": v(-30, -11.25) * mm, "construction": true});
            skCircle(sketch, "E226.MirrorC", {"center": v(67.5, -11.25) * mm, "radius": 1.5 * mm});
            skLineSegment(sketch, "E227.MirrorCS", {"start": v(-75, -3.75) * mm, "end": v(-75, -11.25) * mm, "construction": true});
            skCircle(sketch, "E228.MirrorC", {"center": v(0, -86.25) * mm, "radius": 1.5 * mm});
            skCircle(sketch, "E229.MirrorC", {"center": v(-75, -11.25) * mm, "radius": 1.5 * mm});
            skCircle(sketch, "E230.MirrorC", {"center": v(60, -3.75) * mm, "radius": 1.5 * mm});
            skCircle(sketch, "E231.MirrorC", {"center": v(67.5, -3.75) * mm, "radius": 1.5 * mm});
            skLineSegment(sketch, "E232.MirrorCS", {"start": v(30, -3.75) * mm, "end": v(30, -11.25) * mm, "construction": true});
            skCircle(sketch, "E233.MirrorC", {"center": v(-15, -3.75) * mm, "radius": 1.5 * mm});
            skLineSegment(sketch, "E234.MirrorCS", {"start": v(52.5, -3.75) * mm, "end": v(52.5, -11.25) * mm, "construction": true});
            skCircle(sketch, "E235.MirrorC", {"center": v(15, -11.25) * mm, "radius": 1.5 * mm});
            skLineSegment(sketch, "E236.MirrorCS", {"start": v(45, -3.75) * mm, "end": v(45, -11.25) * mm, "construction": true});
            skCircle(sketch, "E237.MirrorC", {"center": v(0, -63.75) * mm, "radius": 1.5 * mm});
            skCircle(sketch, "E238.MirrorC", {"center": v(-60, -3.75) * mm, "radius": 1.5 * mm});
            skCircle(sketch, "E239.MirrorC", {"center": v(7.5, -11.25) * mm, "radius": 1.5 * mm});
            skCircle(sketch, "E240.MirrorC", {"center": v(15, -3.75) * mm, "radius": 1.5 * mm});
            skCircle(sketch, "E241.MirrorC", {"center": v(-37.5, -3.75) * mm, "radius": 1.5 * mm});
            skLineSegment(sketch, "E242.MirrorCS", {"start": v(7.5, -3.75) * mm, "end": v(7.5, -11.25) * mm, "construction": true});
            skLineSegment(sketch, "E243.MirrorCS", {"start": v(0, -92.25) * mm, "end": v(0, -95.25) * mm});
            skCircle(sketch, "E244.MirrorC", {"center": v(-67.5, -11.25) * mm, "radius": 1.5 * mm});
            skCircle(sketch, "E245.MirrorC", {"center": v(37.5, -11.25) * mm, "radius": 1.5 * mm});
            skLineSegment(sketch, "E246.MirrorCS", {"start": v(-22.5, -3.75) * mm, "end": v(-22.5, -11.25) * mm, "construction": true});
            skCircle(sketch, "E247.MirrorC", {"center": v(-45, -11.25) * mm, "radius": 1.5 * mm});
            skCircle(sketch, "E248.MirrorC", {"center": v(-82.5, -3.75) * mm, "radius": 1.5 * mm});
            skLineSegment(sketch, "E249.MirrorCS", {"start": v(-37.5, -3.75) * mm, "end": v(-37.5, -11.25) * mm, "construction": true});
            skCircle(sketch, "E250.MirrorC", {"center": v(-30, -11.25) * mm, "radius": 1.5 * mm});
            skLineSegment(sketch, "E251.MirrorCS", {"start": v(-67.5, -3.75) * mm, "end": v(-67.5, -11.25) * mm, "construction": true});
            skLineSegment(sketch, "E252.MirrorCS", {"start": v(0, -3.75) * mm, "end": v(0, -11.25) * mm, "construction": true});
            skCircle(sketch, "E253.MirrorC", {"center": v(82.5, -3.75) * mm, "radius": 1.5 * mm});
            skCircle(sketch, "E254.MirrorC", {"center": v(30, -11.25) * mm, "radius": 1.5 * mm});
            skCircle(sketch, "E255.MirrorC", {"center": v(-22.5, -11.25) * mm, "radius": 1.5 * mm});
            skCircle(sketch, "E256.MirrorC", {"center": v(-37.5, -11.25) * mm, "radius": 1.5 * mm});
            skLineSegment(sketch, "E257.MirrorCS", {"start": v(0, -62.25) * mm, "end": v(0, -65.25) * mm});
            skCircle(sketch, "E258.MirrorC", {"center": v(22.5, -3.75) * mm, "radius": 1.5 * mm});
            skLineSegment(sketch, "E259.MirrorCS", {"start": v(-82.5, -3.75) * mm, "end": v(-82.5, -11.25) * mm, "construction": true});
            skLineSegment(sketch, "E260.MirrorCS", {"start": v(75, -3.75) * mm, "end": v(75, -11.25) * mm, "construction": true});
            skLineSegment(sketch, "E261.MirrorCS", {"start": v(-45, -3.75) * mm, "end": v(-45, -11.25) * mm, "construction": true});
            skLineSegment(sketch, "E262.MirrorCS", {"start": v(-52.5, -3.75) * mm, "end": v(-52.5, -11.25) * mm, "construction": true});
            skCircle(sketch, "E263.MirrorC", {"center": v(-75, -3.75) * mm, "radius": 1.5 * mm});
            skCircle(sketch, "E264.MirrorC", {"center": v(-7.5, -3.75) * mm, "radius": 1.5 * mm});
            skCircle(sketch, "E265.MirrorC", {"center": v(-15, -11.25) * mm, "radius": 1.5 * mm});
            skCircle(sketch, "E266.MirrorC", {"center": v(45, -3.75) * mm, "radius": 1.5 * mm});
            skCircle(sketch, "E267.MirrorC", {"center": v(0, -48.75) * mm, "radius": 1.5 * mm});
            skCircle(sketch, "E268.MirrorC", {"center": v(-22.5, -3.75) * mm, "radius": 1.5 * mm});
            skCircle(sketch, "E269.MirrorC", {"center": v(-52.5, -3.75) * mm, "radius": 1.5 * mm});
            skLineSegment(sketch, "E270.MirrorCS", {"start": v(67.5, -3.75) * mm, "end": v(67.5, -11.25) * mm, "construction": true});
            skCircle(sketch, "E271.MirrorC", {"center": v(0, -93.75) * mm, "radius": 1.5 * mm});
            skLineSegment(sketch, "E272.MirrorCS", {"start": v(82.5, -3.75) * mm, "end": v(82.5, -11.25) * mm, "construction": true});
            skCircle(sketch, "E273.MirrorC", {"center": v(60, -11.25) * mm, "radius": 1.5 * mm});
            skLineSegment(sketch, "E274.MirrorCS", {"start": v(-15, -3.75) * mm, "end": v(-15, -11.25) * mm, "construction": true});
            skCircle(sketch, "E275.MirrorC", {"center": v(-45, -3.75) * mm, "radius": 1.5 * mm});
            skCircle(sketch, "E276.MirrorC", {"center": v(22.5, -11.25) * mm, "radius": 1.5 * mm});
            skLineSegment(sketch, "E277.MirrorCS", {"start": v(-7.5, -3.75) * mm, "end": v(-7.5, -11.25) * mm, "construction": true});
            skLineSegment(sketch, "E278.MirrorCS", {"start": v(15, -3.75) * mm, "end": v(15, -11.25) * mm, "construction": true});
            skCircle(sketch, "E279.MirrorC", {"center": v(-60, -11.25) * mm, "radius": 1.5 * mm});
            skCircle(sketch, "E280.MirrorC", {"center": v(0, -11.25) * mm, "radius": 1.5 * mm});
            skCircle(sketch, "E281.MirrorC", {"center": v(-30, -3.75) * mm, "radius": 1.5 * mm});
            skCircle(sketch, "E282.MirrorC", {"center": v(-52.5, -11.25) * mm, "radius": 1.5 * mm});
            skCircle(sketch, "E283.MirrorC", {"center": v(-7.5, -11.25) * mm, "radius": 1.5 * mm});
            skLineSegment(sketch, "E284.MirrorCS", {"start": v(37.5, -3.75) * mm, "end": v(37.5, -11.25) * mm, "construction": true});
            skCircle(sketch, "E285.MirrorC", {"center": v(52.5, -3.75) * mm, "radius": 1.5 * mm});
            skCircle(sketch, "E286.MirrorC", {"center": v(0, -71.25) * mm, "radius": 1.5 * mm});
            skCircle(sketch, "E287.MirrorC", {"center": v(37.5, -3.75) * mm, "radius": 1.5 * mm});
            skCircle(sketch, "E288.MirrorC", {"center": v(75, -11.25) * mm, "radius": 1.5 * mm});
            skCircle(sketch, "E289.MirrorC", {"center": v(30, -3.75) * mm, "radius": 1.5 * mm});
            skLineSegment(sketch, "E290.MirrorCS", {"start": v(60, -3.75) * mm, "end": v(60, -11.25) * mm, "construction": true});
            skCircle(sketch, "E291.MirrorC", {"center": v(-30, -101.25) * mm, "radius": 1.5 * mm});
            skCircle(sketch, "E292.MirrorC", {"center": v(60, -71.25) * mm, "radius": 1.5 * mm});
            skCircle(sketch, "E293.MirrorC", {"center": v(-45, -26.25) * mm, "radius": 1.5 * mm});
            skCircle(sketch, "E294.MirrorC", {"center": v(-37.5, -33.75) * mm, "radius": 1.5 * mm});
            skCircle(sketch, "E295.MirrorC", {"center": v(-45, -86.25) * mm, "radius": 1.5 * mm});
            skCircle(sketch, "E296.MirrorC", {"center": v(-30, -41.25) * mm, "radius": 1.5 * mm});
            skCircle(sketch, "E297.MirrorC", {"center": v(-60, -93.75) * mm, "radius": 1.5 * mm});
            skCircle(sketch, "E298.MirrorC", {"center": v(82.5, -93.75) * mm, "radius": 1.5 * mm});
            skCircle(sketch, "E299.MirrorC", {"center": v(45, -93.75) * mm, "radius": 1.5 * mm});
            skCircle(sketch, "E300.MirrorC", {"center": v(37.5, -71.25) * mm, "radius": 1.5 * mm});
            skCircle(sketch, "E301.MirrorC", {"center": v(75, -26.25) * mm, "radius": 1.5 * mm});
            skCircle(sketch, "E302.MirrorC", {"center": v(-45, -71.25) * mm, "radius": 1.5 * mm});
            skCircle(sketch, "E303.MirrorC", {"center": v(-52.5, -101.25) * mm, "radius": 1.5 * mm});
            skCircle(sketch, "E304.MirrorC", {"center": v(60, -26.25) * mm, "radius": 1.5 * mm});
            skCircle(sketch, "E305.MirrorC", {"center": v(-75, -48.75) * mm, "radius": 1.5 * mm});
            skCircle(sketch, "E306.MirrorC", {"center": v(-15, -101.25) * mm, "radius": 1.5 * mm});
            skCircle(sketch, "E307.MirrorC", {"center": v(-82.5, -63.75) * mm, "radius": 1.5 * mm});
            skCircle(sketch, "E308.MirrorC", {"center": v(-60, -33.75) * mm, "radius": 1.5 * mm});
            skCircle(sketch, "E309.MirrorC", {"center": v(-22.5, -108.75) * mm, "radius": 1.5 * mm});
            skCircle(sketch, "E310.MirrorC", {"center": v(-30, -18.75) * mm, "radius": 1.5 * mm});
            skCircle(sketch, "E311.MirrorC", {"center": v(75, -63.75) * mm, "radius": 1.5 * mm});
            skCircle(sketch, "E312.MirrorC", {"center": v(15, -48.75) * mm, "radius": 1.5 * mm});
            skCircle(sketch, "E313.MirrorC", {"center": v(-15, -33.75) * mm, "radius": 1.5 * mm});
            skCircle(sketch, "E314.MirrorC", {"center": v(-37.5, -18.75) * mm, "radius": 1.5 * mm});
            skCircle(sketch, "E315.MirrorC", {"center": v(67.5, -48.75) * mm, "radius": 1.5 * mm});
            skCircle(sketch, "E316.MirrorC", {"center": v(37.5, -48.75) * mm, "radius": 1.5 * mm});
            skCircle(sketch, "E317.MirrorC", {"center": v(52.5, -26.25) * mm, "radius": 1.5 * mm});
            skCircle(sketch, "E318.MirrorC", {"center": v(82.5, -108.75) * mm, "radius": 1.5 * mm});
            skCircle(sketch, "E319.MirrorC", {"center": v(60, -93.75) * mm, "radius": 1.5 * mm});
            skCircle(sketch, "E320.MirrorC", {"center": v(-30, -26.25) * mm, "radius": 1.5 * mm});
            skCircle(sketch, "E321.MirrorC", {"center": v(-7.5, -26.25) * mm, "radius": 1.5 * mm});
            skCircle(sketch, "E322.MirrorC", {"center": v(-75, -41.25) * mm, "radius": 1.5 * mm});
            skCircle(sketch, "E323.MirrorC", {"center": v(-37.5, -41.25) * mm, "radius": 1.5 * mm});
            skCircle(sketch, "E324.MirrorC", {"center": v(-22.5, -18.75) * mm, "radius": 1.5 * mm});
            skCircle(sketch, "E325.MirrorC", {"center": v(22.5, -63.75) * mm, "radius": 1.5 * mm});
            skCircle(sketch, "E326.MirrorC", {"center": v(60, -78.75) * mm, "radius": 1.5 * mm});
            skCircle(sketch, "E327.MirrorC", {"center": v(-30, -86.25) * mm, "radius": 1.5 * mm});
            skCircle(sketch, "E328.MirrorC", {"center": v(-15, -63.75) * mm, "radius": 1.5 * mm});
            skCircle(sketch, "E329.MirrorC", {"center": v(-82.5, -48.75) * mm, "radius": 1.5 * mm});
            skCircle(sketch, "E330.MirrorC", {"center": v(67.5, -56.25) * mm, "radius": 1.5 * mm});
            skCircle(sketch, "E331.MirrorC", {"center": v(-37.5, -86.25) * mm, "radius": 1.5 * mm});
            skCircle(sketch, "E332.MirrorC", {"center": v(52.5, -48.75) * mm, "radius": 1.5 * mm});
            skCircle(sketch, "E333.MirrorC", {"center": v(45, -56.25) * mm, "radius": 1.5 * mm});
            skCircle(sketch, "E334.MirrorC", {"center": v(-52.5, -63.75) * mm, "radius": 1.5 * mm});
            skCircle(sketch, "E335.MirrorC", {"center": v(-60, -56.25) * mm, "radius": 1.5 * mm});
            skCircle(sketch, "E336.MirrorC", {"center": v(-67.5, -71.25) * mm, "radius": 1.5 * mm});
            skCircle(sketch, "E337.MirrorC", {"center": v(37.5, -18.75) * mm, "radius": 1.5 * mm});
            skCircle(sketch, "E338.MirrorC", {"center": v(75, -93.75) * mm, "radius": 1.5 * mm});
            skCircle(sketch, "E339.MirrorC", {"center": v(-67.5, -33.75) * mm, "radius": 1.5 * mm});
            skCircle(sketch, "E340.MirrorC", {"center": v(-22.5, -93.75) * mm, "radius": 1.5 * mm});
            skCircle(sketch, "E341.MirrorC", {"center": v(-22.5, -26.25) * mm, "radius": 1.5 * mm});
            skCircle(sketch, "E342.MirrorC", {"center": v(-30, -56.25) * mm, "radius": 1.5 * mm});
            skCircle(sketch, "E343.MirrorC", {"center": v(75, -71.25) * mm, "radius": 1.5 * mm});
            skCircle(sketch, "E344.MirrorC", {"center": v(-60, -86.25) * mm, "radius": 1.5 * mm});
            skCircle(sketch, "E345.MirrorC", {"center": v(45, -63.75) * mm, "radius": 1.5 * mm});
            skCircle(sketch, "E346.MirrorC", {"center": v(30, -41.25) * mm, "radius": 1.5 * mm});
            skCircle(sketch, "E347.MirrorC", {"center": v(37.5, -63.75) * mm, "radius": 1.5 * mm});
            skCircle(sketch, "E348.MirrorC", {"center": v(-52.5, -18.75) * mm, "radius": 1.5 * mm});
            skCircle(sketch, "E349.MirrorC", {"center": v(-22.5, -78.75) * mm, "radius": 1.5 * mm});
            skCircle(sketch, "E350.MirrorC", {"center": v(52.5, -33.75) * mm, "radius": 1.5 * mm});
            skCircle(sketch, "E351.MirrorC", {"center": v(-67.5, -86.25) * mm, "radius": 1.5 * mm});
            skCircle(sketch, "E352.MirrorC", {"center": v(-52.5, -26.25) * mm, "radius": 1.5 * mm});
            skCircle(sketch, "E353.MirrorC", {"center": v(-22.5, -56.25) * mm, "radius": 1.5 * mm});
            skCircle(sketch, "E354.MirrorC", {"center": v(60, -41.25) * mm, "radius": 1.5 * mm});
            skCircle(sketch, "E355.MirrorC", {"center": v(60, -63.75) * mm, "radius": 1.5 * mm});
            skCircle(sketch, "E356.MirrorC", {"center": v(30, -86.25) * mm, "radius": 1.5 * mm});
            skCircle(sketch, "E357.MirrorC", {"center": v(-7.5, -56.25) * mm, "radius": 1.5 * mm});
            skCircle(sketch, "E358.MirrorC", {"center": v(22.5, -101.25) * mm, "radius": 1.5 * mm});
            skCircle(sketch, "E359.MirrorC", {"center": v(30, -56.25) * mm, "radius": 1.5 * mm});
            skCircle(sketch, "E360.MirrorC", {"center": v(67.5, -101.25) * mm, "radius": 1.5 * mm});
            skCircle(sketch, "E361.MirrorC", {"center": v(-67.5, -18.75) * mm, "radius": 1.5 * mm});
            skCircle(sketch, "E362.MirrorC", {"center": v(-60, -101.25) * mm, "radius": 1.5 * mm});
            skCircle(sketch, "E363.MirrorC", {"center": v(52.5, -71.25) * mm, "radius": 1.5 * mm});
            skCircle(sketch, "E364.MirrorC", {"center": v(-45, -48.75) * mm, "radius": 1.5 * mm});
            skCircle(sketch, "E365.MirrorC", {"center": v(45, -48.75) * mm, "radius": 1.5 * mm});
            skCircle(sketch, "E366.MirrorC", {"center": v(-67.5, -48.75) * mm, "radius": 1.5 * mm});
            skCircle(sketch, "E367.MirrorC", {"center": v(-45, -41.25) * mm, "radius": 1.5 * mm});
            skCircle(sketch, "E368.MirrorC", {"center": v(-52.5, -56.25) * mm, "radius": 1.5 * mm});
            skCircle(sketch, "E369.MirrorC", {"center": v(-15, -48.75) * mm, "radius": 1.5 * mm});
            skCircle(sketch, "E370.MirrorC", {"center": v(-82.5, -108.75) * mm, "radius": 1.5 * mm});
            skCircle(sketch, "E371.MirrorC", {"center": v(-67.5, -56.25) * mm, "radius": 1.5 * mm});
            skCircle(sketch, "E372.MirrorC", {"center": v(15, -33.75) * mm, "radius": 1.5 * mm});
            skCircle(sketch, "E373.MirrorC", {"center": v(-45, -33.75) * mm, "radius": 1.5 * mm});
            skCircle(sketch, "E374.MirrorC", {"center": v(-52.5, -33.75) * mm, "radius": 1.5 * mm});
            skCircle(sketch, "E375.MirrorC", {"center": v(22.5, -108.75) * mm, "radius": 1.5 * mm});
            skCircle(sketch, "E376.MirrorC", {"center": v(37.5, -26.25) * mm, "radius": 1.5 * mm});
            skCircle(sketch, "E377.MirrorC", {"center": v(45, -101.25) * mm, "radius": 1.5 * mm});
            skCircle(sketch, "E378.MirrorC", {"center": v(67.5, -71.25) * mm, "radius": 1.5 * mm});
            skCircle(sketch, "E379.MirrorC", {"center": v(45, -41.25) * mm, "radius": 1.5 * mm});
            skCircle(sketch, "E380.MirrorC", {"center": v(67.5, -26.25) * mm, "radius": 1.5 * mm});
            skCircle(sketch, "E381.MirrorC", {"center": v(-7.5, -86.25) * mm, "radius": 1.5 * mm});
            skCircle(sketch, "E382.MirrorC", {"center": v(7.5, -33.75) * mm, "radius": 1.5 * mm});
            skCircle(sketch, "E383.MirrorC", {"center": v(-37.5, -101.25) * mm, "radius": 1.5 * mm});
            skCircle(sketch, "E384.MirrorC", {"center": v(-52.5, -108.75) * mm, "radius": 1.5 * mm});
            skCircle(sketch, "E385.MirrorC", {"center": v(60, -33.75) * mm, "radius": 1.5 * mm});
            skCircle(sketch, "E386.MirrorC", {"center": v(30, -33.75) * mm, "radius": 1.5 * mm});
            skCircle(sketch, "E387.MirrorC", {"center": v(7.5, -108.75) * mm, "radius": 1.5 * mm});
            skCircle(sketch, "E388.MirrorC", {"center": v(75, -33.75) * mm, "radius": 1.5 * mm});
            skCircle(sketch, "E389.MirrorC", {"center": v(-82.5, -18.75) * mm, "radius": 1.5 * mm});
            skCircle(sketch, "E390.MirrorC", {"center": v(52.5, -18.75) * mm, "radius": 1.5 * mm});
            skCircle(sketch, "E391.MirrorC", {"center": v(15, -26.25) * mm, "radius": 1.5 * mm});
            skCircle(sketch, "E392.MirrorC", {"center": v(52.5, -93.75) * mm, "radius": 1.5 * mm});
            skCircle(sketch, "E393.MirrorC", {"center": v(22.5, -56.25) * mm, "radius": 1.5 * mm});
            skCircle(sketch, "E394.MirrorC", {"center": v(-15, -18.75) * mm, "radius": 1.5 * mm});
            skCircle(sketch, "E395.MirrorC", {"center": v(-67.5, -101.25) * mm, "radius": 1.5 * mm});
            skCircle(sketch, "E396.MirrorC", {"center": v(75, -56.25) * mm, "radius": 1.5 * mm});
            skCircle(sketch, "E397.MirrorC", {"center": v(52.5, -86.25) * mm, "radius": 1.5 * mm});
            skCircle(sketch, "E398.MirrorC", {"center": v(37.5, -101.25) * mm, "radius": 1.5 * mm});
            skCircle(sketch, "E399.MirrorC", {"center": v(67.5, -108.75) * mm, "radius": 1.5 * mm});
            skCircle(sketch, "E400.MirrorC", {"center": v(-52.5, -71.25) * mm, "radius": 1.5 * mm});
            skCircle(sketch, "E401.MirrorC", {"center": v(-60, -71.25) * mm, "radius": 1.5 * mm});
            skCircle(sketch, "E402.MirrorC", {"center": v(-7.5, -71.25) * mm, "radius": 1.5 * mm});
            skCircle(sketch, "E403.MirrorC", {"center": v(22.5, -26.25) * mm, "radius": 1.5 * mm});
            skCircle(sketch, "E404.MirrorC", {"center": v(45, -71.25) * mm, "radius": 1.5 * mm});
            skCircle(sketch, "E405.MirrorC", {"center": v(67.5, -33.75) * mm, "radius": 1.5 * mm});
            skCircle(sketch, "E406.MirrorC", {"center": v(45, -78.75) * mm, "radius": 1.5 * mm});
            skCircle(sketch, "E407.MirrorC", {"center": v(45, -33.75) * mm, "radius": 1.5 * mm});
            skCircle(sketch, "E408.MirrorC", {"center": v(37.5, -56.25) * mm, "radius": 1.5 * mm});
            skCircle(sketch, "E409.MirrorC", {"center": v(52.5, -78.75) * mm, "radius": 1.5 * mm});
            skCircle(sketch, "E410.MirrorC", {"center": v(60, -86.25) * mm, "radius": 1.5 * mm});
            skCircle(sketch, "E411.MirrorC", {"center": v(75, -86.25) * mm, "radius": 1.5 * mm});
            skCircle(sketch, "E412.MirrorC", {"center": v(75, -101.25) * mm, "radius": 1.5 * mm});
            skCircle(sketch, "E413.MirrorC", {"center": v(75, -41.25) * mm, "radius": 1.5 * mm});
            skCircle(sketch, "E414.MirrorC", {"center": v(-22.5, -48.75) * mm, "radius": 1.5 * mm});
            skCircle(sketch, "E415.MirrorC", {"center": v(52.5, -41.25) * mm, "radius": 1.5 * mm});
            skCircle(sketch, "E416.MirrorC", {"center": v(-30, -71.25) * mm, "radius": 1.5 * mm});
            skCircle(sketch, "E417.MirrorC", {"center": v(15, -93.75) * mm, "radius": 1.5 * mm});
            skCircle(sketch, "E418.MirrorC", {"center": v(-75, -78.75) * mm, "radius": 1.5 * mm});
            skCircle(sketch, "E419.MirrorC", {"center": v(15, -56.25) * mm, "radius": 1.5 * mm});
            skCircle(sketch, "E420.MirrorC", {"center": v(-67.5, -41.25) * mm, "radius": 1.5 * mm});
            skCircle(sketch, "E421.MirrorC", {"center": v(-7.5, -41.25) * mm, "radius": 1.5 * mm});
            skCircle(sketch, "E422.MirrorC", {"center": v(45, -18.75) * mm, "radius": 1.5 * mm});
            skCircle(sketch, "E423.MirrorC", {"center": v(-7.5, -93.75) * mm, "radius": 1.5 * mm});
            skCircle(sketch, "E424.MirrorC", {"center": v(30, -18.75) * mm, "radius": 1.5 * mm});
            skCircle(sketch, "E425.MirrorC", {"center": v(15, -18.75) * mm, "radius": 1.5 * mm});
            skCircle(sketch, "E426.MirrorC", {"center": v(-37.5, -56.25) * mm, "radius": 1.5 * mm});
            skCircle(sketch, "E427.MirrorC", {"center": v(-67.5, -78.75) * mm, "radius": 1.5 * mm});
            skCircle(sketch, "E428.MirrorC", {"center": v(22.5, -78.75) * mm, "radius": 1.5 * mm});
            skCircle(sketch, "E429.MirrorC", {"center": v(22.5, -71.25) * mm, "radius": 1.5 * mm});
            skCircle(sketch, "E430.MirrorC", {"center": v(-22.5, -86.25) * mm, "radius": 1.5 * mm});
            skCircle(sketch, "E431.MirrorC", {"center": v(-7.5, -101.25) * mm, "radius": 1.5 * mm});
            skCircle(sketch, "E432.MirrorC", {"center": v(82.5, -48.75) * mm, "radius": 1.5 * mm});
            skCircle(sketch, "E433.MirrorC", {"center": v(-37.5, -93.75) * mm, "radius": 1.5 * mm});
            skCircle(sketch, "E434.MirrorC", {"center": v(-15, -56.25) * mm, "radius": 1.5 * mm});
            skCircle(sketch, "E435.MirrorC", {"center": v(-45, -101.25) * mm, "radius": 1.5 * mm});
            skCircle(sketch, "E436.MirrorC", {"center": v(37.5, -41.25) * mm, "radius": 1.5 * mm});
            skCircle(sketch, "E437.MirrorC", {"center": v(-52.5, -78.75) * mm, "radius": 1.5 * mm});
            skCircle(sketch, "E438.MirrorC", {"center": v(22.5, -18.75) * mm, "radius": 1.5 * mm});
            skCircle(sketch, "E439.MirrorC", {"center": v(-37.5, -78.75) * mm, "radius": 1.5 * mm});
            skCircle(sketch, "E440.MirrorC", {"center": v(67.5, -93.75) * mm, "radius": 1.5 * mm});
            skCircle(sketch, "E441.MirrorC", {"center": v(15, -71.25) * mm, "radius": 1.5 * mm});
            skCircle(sketch, "E442.MirrorC", {"center": v(-60, -63.75) * mm, "radius": 1.5 * mm});
            skCircle(sketch, "E443.MirrorC", {"center": v(-60, -26.25) * mm, "radius": 1.5 * mm});
            skCircle(sketch, "E444.MirrorC", {"center": v(37.5, -33.75) * mm, "radius": 1.5 * mm});
            skCircle(sketch, "E445.MirrorC", {"center": v(-52.5, -93.75) * mm, "radius": 1.5 * mm});
            skCircle(sketch, "E446.MirrorC", {"center": v(37.5, -78.75) * mm, "radius": 1.5 * mm});
            skCircle(sketch, "E447.MirrorC", {"center": v(-82.5, -78.75) * mm, "radius": 1.5 * mm});
            skCircle(sketch, "E448.MirrorC", {"center": v(7.5, -86.25) * mm, "radius": 1.5 * mm});
            skCircle(sketch, "E449.MirrorC", {"center": v(-75, -26.25) * mm, "radius": 1.5 * mm});
            skCircle(sketch, "E450.MirrorC", {"center": v(-30, -48.75) * mm, "radius": 1.5 * mm});
            skCircle(sketch, "E451.MirrorC", {"center": v(-30, -63.75) * mm, "radius": 1.5 * mm});
            skCircle(sketch, "E452.MirrorC", {"center": v(-60, -41.25) * mm, "radius": 1.5 * mm});
            skCircle(sketch, "E453.MirrorC", {"center": v(67.5, -18.75) * mm, "radius": 1.5 * mm});
            skCircle(sketch, "E454.MirrorC", {"center": v(82.5, -33.75) * mm, "radius": 1.5 * mm});
            skCircle(sketch, "E455.MirrorC", {"center": v(15, -63.75) * mm, "radius": 1.5 * mm});
            skCircle(sketch, "E456.MirrorC", {"center": v(15, -78.75) * mm, "radius": 1.5 * mm});
            skCircle(sketch, "E457.MirrorC", {"center": v(60, -48.75) * mm, "radius": 1.5 * mm});
            skCircle(sketch, "E458.MirrorC", {"center": v(-52.5, -48.75) * mm, "radius": 1.5 * mm});
            skCircle(sketch, "E459.MirrorC", {"center": v(37.5, -93.75) * mm, "radius": 1.5 * mm});
            skCircle(sketch, "E460.MirrorC", {"center": v(-7.5, -78.75) * mm, "radius": 1.5 * mm});
            skCircle(sketch, "E461.MirrorC", {"center": v(-37.5, -63.75) * mm, "radius": 1.5 * mm});
            skCircle(sketch, "E462.MirrorC", {"center": v(-82.5, -33.75) * mm, "radius": 1.5 * mm});
            skCircle(sketch, "E463.MirrorC", {"center": v(-37.5, -48.75) * mm, "radius": 1.5 * mm});
            skCircle(sketch, "E464.MirrorC", {"center": v(-75, -33.75) * mm, "radius": 1.5 * mm});
            skCircle(sketch, "E465.MirrorC", {"center": v(30, -101.25) * mm, "radius": 1.5 * mm});
            skCircle(sketch, "E466.MirrorC", {"center": v(45, -86.25) * mm, "radius": 1.5 * mm});
            skCircle(sketch, "E467.MirrorC", {"center": v(-7.5, -33.75) * mm, "radius": 1.5 * mm});
            skCircle(sketch, "E468.MirrorC", {"center": v(22.5, -86.25) * mm, "radius": 1.5 * mm});
            skCircle(sketch, "E469.MirrorC", {"center": v(-67.5, -26.25) * mm, "radius": 1.5 * mm});
            skCircle(sketch, "E470.MirrorC", {"center": v(7.5, -78.75) * mm, "radius": 1.5 * mm});
            skCircle(sketch, "E471.MirrorC", {"center": v(-45, -18.75) * mm, "radius": 1.5 * mm});
            skCircle(sketch, "E472.MirrorC", {"center": v(22.5, -93.75) * mm, "radius": 1.5 * mm});
            skCircle(sketch, "E473.MirrorC", {"center": v(-52.5, -41.25) * mm, "radius": 1.5 * mm});
            skCircle(sketch, "E474.MirrorC", {"center": v(22.5, -33.75) * mm, "radius": 1.5 * mm});
            skCircle(sketch, "E475.MirrorC", {"center": v(-22.5, -33.75) * mm, "radius": 1.5 * mm});
            skCircle(sketch, "E476.MirrorC", {"center": v(30, -26.25) * mm, "radius": 1.5 * mm});
            skCircle(sketch, "E477.MirrorC", {"center": v(-7.5, -63.75) * mm, "radius": 1.5 * mm});
            skCircle(sketch, "E478.MirrorC", {"center": v(75, -18.75) * mm, "radius": 1.5 * mm});
            skCircle(sketch, "E479.MirrorC", {"center": v(-75, -63.75) * mm, "radius": 1.5 * mm});
            skCircle(sketch, "E480.MirrorC", {"center": v(-60, -48.75) * mm, "radius": 1.5 * mm});
            skCircle(sketch, "E481.MirrorC", {"center": v(-37.5, -26.25) * mm, "radius": 1.5 * mm});
            skCircle(sketch, "E482.MirrorC", {"center": v(67.5, -86.25) * mm, "radius": 1.5 * mm});
            skCircle(sketch, "E483.MirrorC", {"center": v(0, -41.25) * mm, "radius": 1.5 * mm});
            skCircle(sketch, "E484.MirrorC", {"center": v(7.5, -18.75) * mm, "radius": 1.5 * mm});
            skCircle(sketch, "E485.MirrorC", {"center": v(-60, -78.75) * mm, "radius": 1.5 * mm});
            skCircle(sketch, "E486.MirrorC", {"center": v(-15, -78.75) * mm, "radius": 1.5 * mm});
            skCircle(sketch, "E487.MirrorC", {"center": v(-22.5, -101.25) * mm, "radius": 1.5 * mm});
            skCircle(sketch, "E488.MirrorC", {"center": v(15, -41.25) * mm, "radius": 1.5 * mm});
            skCircle(sketch, "E489.MirrorC", {"center": v(-22.5, -63.75) * mm, "radius": 1.5 * mm});
            skCircle(sketch, "E490.MirrorC", {"center": v(30, -48.75) * mm, "radius": 1.5 * mm});
            skCircle(sketch, "E491.MirrorC", {"center": v(30, -78.75) * mm, "radius": 1.5 * mm});
            skCircle(sketch, "E492.MirrorC", {"center": v(-52.5, -86.25) * mm, "radius": 1.5 * mm});
            skCircle(sketch, "E493.MirrorC", {"center": v(-75, -71.25) * mm, "radius": 1.5 * mm});
            skCircle(sketch, "E494.MirrorC", {"center": v(52.5, -63.75) * mm, "radius": 1.5 * mm});
            skCircle(sketch, "E495.MirrorC", {"center": v(-67.5, -63.75) * mm, "radius": 1.5 * mm});
            skCircle(sketch, "E496.MirrorC", {"center": v(67.5, -63.75) * mm, "radius": 1.5 * mm});
            skCircle(sketch, "E497.MirrorC", {"center": v(-82.5, -93.75) * mm, "radius": 1.5 * mm});
            skCircle(sketch, "E498.MirrorC", {"center": v(52.5, -108.75) * mm, "radius": 1.5 * mm});
            skCircle(sketch, "E499.MirrorC", {"center": v(7.5, -71.25) * mm, "radius": 1.5 * mm});
            skCircle(sketch, "E500.MirrorC", {"center": v(-67.5, -108.75) * mm, "radius": 1.5 * mm});
            skCircle(sketch, "E501.MirrorC", {"center": v(45, -26.25) * mm, "radius": 1.5 * mm});
            skCircle(sketch, "E502.MirrorC", {"center": v(7.5, -56.25) * mm, "radius": 1.5 * mm});
            skCircle(sketch, "E503.MirrorC", {"center": v(-45, -56.25) * mm, "radius": 1.5 * mm});
            skCircle(sketch, "E504.MirrorC", {"center": v(60, -101.25) * mm, "radius": 1.5 * mm});
            skCircle(sketch, "E505.MirrorC", {"center": v(-75, -18.75) * mm, "radius": 1.5 * mm});
            skCircle(sketch, "E506.MirrorC", {"center": v(-30, -33.75) * mm, "radius": 1.5 * mm});
            skCircle(sketch, "E507.MirrorC", {"center": v(60, -56.25) * mm, "radius": 1.5 * mm});
            skCircle(sketch, "E508.MirrorC", {"center": v(-60, -18.75) * mm, "radius": 1.5 * mm});
            skCircle(sketch, "E509.MirrorC", {"center": v(7.5, -93.75) * mm, "radius": 1.5 * mm});
            skCircle(sketch, "E510.MirrorC", {"center": v(-45, -78.75) * mm, "radius": 1.5 * mm});
            skCircle(sketch, "E511.MirrorC", {"center": v(75, -48.75) * mm, "radius": 1.5 * mm});
            skCircle(sketch, "E512.MirrorC", {"center": v(37.5, -108.75) * mm, "radius": 1.5 * mm});
            skCircle(sketch, "E513.MirrorC", {"center": v(30, -71.25) * mm, "radius": 1.5 * mm});
            skCircle(sketch, "E514.MirrorC", {"center": v(-75, -101.25) * mm, "radius": 1.5 * mm});
            skCircle(sketch, "E515.MirrorC", {"center": v(75, -78.75) * mm, "radius": 1.5 * mm});
            skCircle(sketch, "E516.MirrorC", {"center": v(-22.5, -71.25) * mm, "radius": 1.5 * mm});
            skCircle(sketch, "E517.MirrorC", {"center": v(-15, -41.25) * mm, "radius": 1.5 * mm});
            skCircle(sketch, "E518.MirrorC", {"center": v(-75, -93.75) * mm, "radius": 1.5 * mm});
            skCircle(sketch, "E519.MirrorC", {"center": v(-15, -86.25) * mm, "radius": 1.5 * mm});
            skCircle(sketch, "E520.MirrorC", {"center": v(-15, -71.25) * mm, "radius": 1.5 * mm});
            skCircle(sketch, "E521.MirrorC", {"center": v(7.5, -26.25) * mm, "radius": 1.5 * mm});
            skCircle(sketch, "E522.MirrorC", {"center": v(22.5, -41.25) * mm, "radius": 1.5 * mm});
            skCircle(sketch, "E523.MirrorC", {"center": v(52.5, -101.25) * mm, "radius": 1.5 * mm});
            skCircle(sketch, "E524.MirrorC", {"center": v(0, -18.75) * mm, "radius": 1.5 * mm});
            skCircle(sketch, "E525.MirrorC", {"center": v(-15, -93.75) * mm, "radius": 1.5 * mm});
            skCircle(sketch, "E526.MirrorC", {"center": v(-7.5, -18.75) * mm, "radius": 1.5 * mm});
            skCircle(sketch, "E527.MirrorC", {"center": v(67.5, -78.75) * mm, "radius": 1.5 * mm});
            skCircle(sketch, "E528.MirrorC", {"center": v(-30, -93.75) * mm, "radius": 1.5 * mm});
            skCircle(sketch, "E529.MirrorC", {"center": v(7.5, -101.25) * mm, "radius": 1.5 * mm});
            skCircle(sketch, "E530.MirrorC", {"center": v(-22.5, -41.25) * mm, "radius": 1.5 * mm});
            skCircle(sketch, "E531.MirrorC", {"center": v(22.5, -48.75) * mm, "radius": 1.5 * mm});
            skCircle(sketch, "E532.MirrorC", {"center": v(82.5, -63.75) * mm, "radius": 1.5 * mm});
            skCircle(sketch, "E533.MirrorC", {"center": v(-7.5, -108.75) * mm, "radius": 1.5 * mm});
            skCircle(sketch, "E534.MirrorC", {"center": v(15, -86.25) * mm, "radius": 1.5 * mm});
            skCircle(sketch, "E535.MirrorC", {"center": v(-75, -86.25) * mm, "radius": 1.5 * mm});
            skCircle(sketch, "E536.MirrorC", {"center": v(82.5, -78.75) * mm, "radius": 1.5 * mm});
            skCircle(sketch, "E537.MirrorC", {"center": v(37.5, -86.25) * mm, "radius": 1.5 * mm});
            skCircle(sketch, "E538.MirrorC", {"center": v(82.5, -18.75) * mm, "radius": 1.5 * mm});
            skCircle(sketch, "E539.MirrorC", {"center": v(-15, -26.25) * mm, "radius": 1.5 * mm});
            skCircle(sketch, "E540.MirrorC", {"center": v(67.5, -41.25) * mm, "radius": 1.5 * mm});
            skCircle(sketch, "E541.MirrorC", {"center": v(-45, -93.75) * mm, "radius": 1.5 * mm});
            skCircle(sketch, "E542.MirrorC", {"center": v(7.5, -63.75) * mm, "radius": 1.5 * mm});
            skCircle(sketch, "E543.MirrorC", {"center": v(60, -18.75) * mm, "radius": 1.5 * mm});
            skCircle(sketch, "E544.MirrorC", {"center": v(7.5, -48.75) * mm, "radius": 1.5 * mm});
            skCircle(sketch, "E545.MirrorC", {"center": v(30, -93.75) * mm, "radius": 1.5 * mm});
            skCircle(sketch, "E546.MirrorC", {"center": v(-67.5, -93.75) * mm, "radius": 1.5 * mm});
            skCircle(sketch, "E547.MirrorC", {"center": v(-45, -63.75) * mm, "radius": 1.5 * mm});
            skCircle(sketch, "E548.MirrorC", {"center": v(-37.5, -71.25) * mm, "radius": 1.5 * mm});
            skCircle(sketch, "E549.MirrorC", {"center": v(15, -101.25) * mm, "radius": 1.5 * mm});
            skCircle(sketch, "E550.MirrorC", {"center": v(52.5, -56.25) * mm, "radius": 1.5 * mm});
            skCircle(sketch, "E551.MirrorC", {"center": v(7.5, -41.25) * mm, "radius": 1.5 * mm});
            skCircle(sketch, "E552.MirrorC", {"center": v(30, -63.75) * mm, "radius": 1.5 * mm});
            skCircle(sketch, "E553.MirrorC", {"center": v(-37.5, -108.75) * mm, "radius": 1.5 * mm});
            skCircle(sketch, "E554.MirrorC", {"center": v(-30, -78.75) * mm, "radius": 1.5 * mm});
            skCircle(sketch, "E555.MirrorC", {"center": v(-7.5, -48.75) * mm, "radius": 1.5 * mm});
            skCircle(sketch, "E556.MirrorC", {"center": v(-75, -56.25) * mm, "radius": 1.5 * mm});
            skLineSegment(sketch, "E557.MirrorCS", {"start": v(0, -39.75) * mm, "end": v(0, -50.25) * mm});
            skLineSegment(sketch, "E558.MirrorCS", {"start": v(0, -3.75) * mm, "end": v(25, -3.75) * mm, "construction": true});
            skSolve(sketch);
        }
        {
            var Q0;
            Q0 = qSketchRegion(id + "F4", true);
            extrude(context, id + "F5", {"entities" : qUnion([Q0]), "operationType" : NewBodyOperationType.REMOVE, "endBound" : BoundingType.THROUGH_ALL, "oppositeDirection" : true, "depth" : 25 * mm, "offsetDistance" : 25 * mm});
        }
    });
